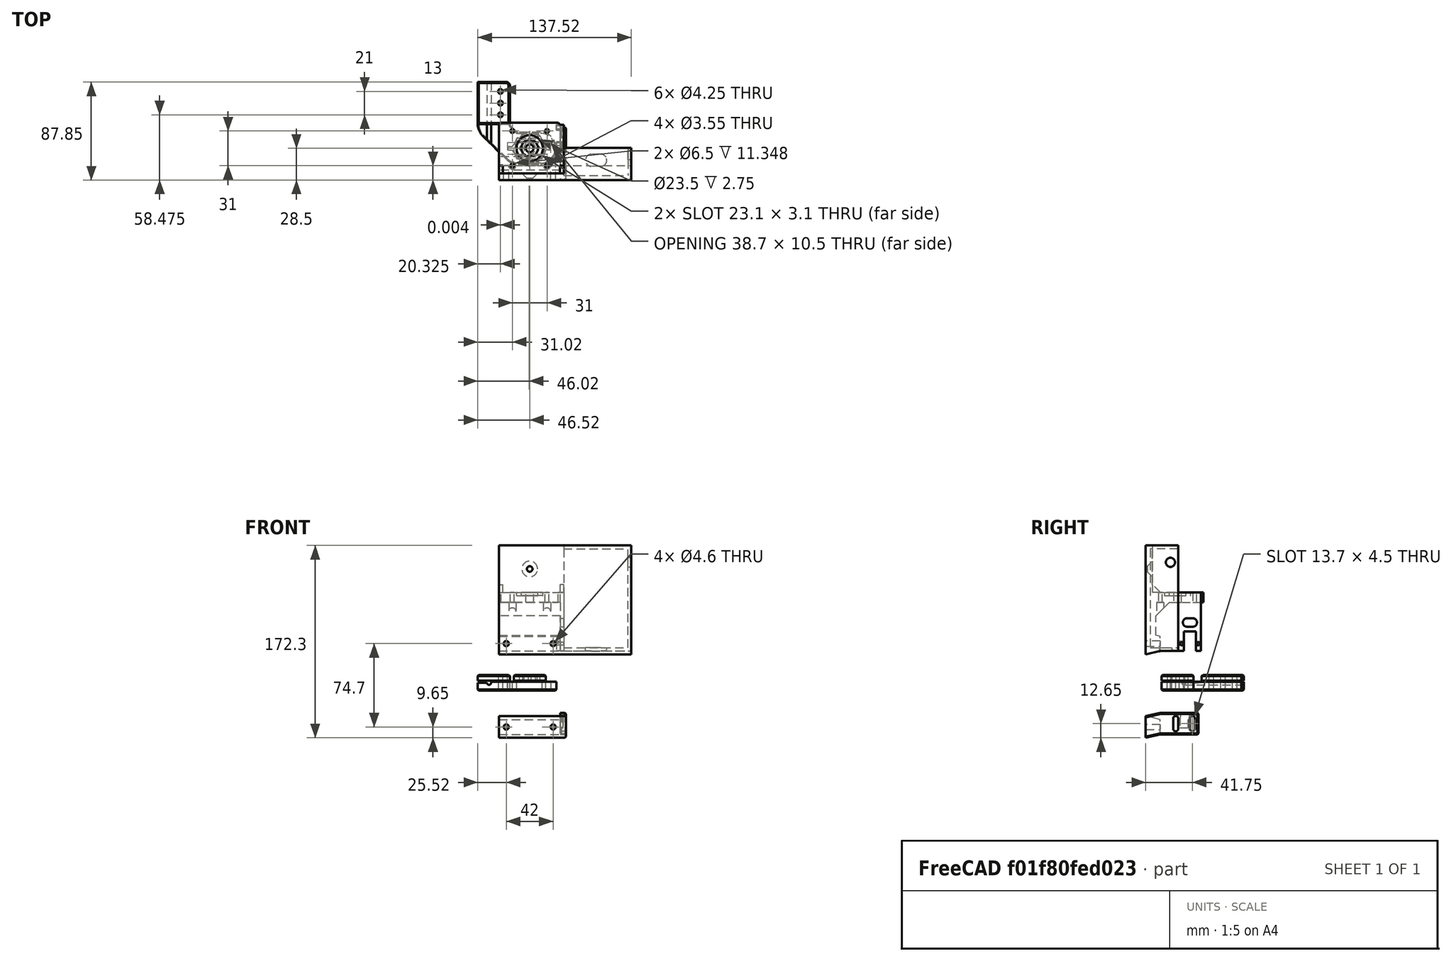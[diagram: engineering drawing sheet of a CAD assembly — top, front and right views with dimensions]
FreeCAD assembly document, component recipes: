
FREECAD ASSEMBLY — COMPONENT RECIPES ("Mount_Mk2")

This assembly document has 5 components, labeled P0..P4 below (a component is one placed body or linked part). 5 of them carry a construction recipe — the FreeCAD feature program that regenerates the part from scratch, quoted from this document or its linked companion documents; the rest are supplied as boundary geometry only. No exploded tour is included for this assembly.
COMPONENT P0 — recipe-attached ("Motor_Mount001", modeled in this document).
Construction recipe (the document's own serialized feature program — sketch geometry with constraints, then the solid features built on it; lengths are millimeters unless a unit is written):

FEATURE [Sketcher::SketchObject] Sketch002
  ArcFitTolerance = 1e-06
  AttachmentSupport = -> [XZ_Plane001]
  FullyConstrained = true
  MakeInternals = false
  MapMode = 5
  Placement = pos=(0,0,0) rot=(1,0,0;1.5708rad)
  sketch-geometry (32):
    g0: LineSegment StartX=0 StartY=0 StartZ=0 EndX=97.6 EndY=0 EndZ=0
    g1: LineSegment StartX=97.6 StartY=0 StartZ=0 EndX=94.6 EndY=13 EndZ=0
    g2: LineSegment StartX=94.6 StartY=13 StartZ=0 EndX=81.3 EndY=13 EndZ=0
    g3: LineSegment StartX=81.3 StartY=13 StartZ=0 EndX=80.3769 EndY=9 EndZ=0
    g4: LineSegment StartX=80.3769 StartY=9 StartZ=0 EndX=51.1 EndY=9 EndZ=0
    g5: LineSegment StartX=51.1 StartY=9 StartZ=0 EndX=51.1 EndY=51.55 EndZ=0
    g6: LineSegment StartX=51.1 StartY=51.55 StartZ=0 EndX=42.1 EndY=51.55 EndZ=0
    g7: LineSegment StartX=42.1 StartY=51.55 StartZ=0 EndX=42.1 EndY=6 EndZ=0
    g8: LineSegment StartX=42.1 StartY=6 StartZ=0 EndX=0 EndY=6 EndZ=0
    g9: LineSegment StartX=0 StartY=6 StartZ=0 EndX=0 EndY=0 EndZ=0
    g10: LineSegment [constr] StartX=94.6 StartY=13 StartZ=0 EndX=97.6 EndY=13 EndZ=0
    g11: LineSegment [constr] StartX=97.6 StartY=13 StartZ=0 EndX=97.6 EndY=0 EndZ=0
    g12: LineSegment [constr] StartX=80.3769 StartY=9 StartZ=0 EndX=78.3 EndY=0 EndZ=0
    g13: LineSegment [constr] StartX=78.3 StartY=0 StartZ=0 EndX=78.3 EndY=13 EndZ=0
    g14: LineSegment [constr] StartX=78.3 StartY=13 StartZ=0 EndX=81.3 EndY=13 EndZ=0
    g15: LineSegment [constr] StartX=81.3 StartY=13 StartZ=0 EndX=81.3 EndY=0 EndZ=0
    g16: LineSegment [constr] StartX=3 StartY=49.55 StartZ=0 EndX=42.3 EndY=49.55 EndZ=0
    g17: LineSegment [constr] StartX=42.3 StartY=7.45 StartZ=0 EndX=3 EndY=7.45 EndZ=0
    g18: LineSegment [constr] StartX=3 StartY=7.45 StartZ=0 EndX=3 EndY=49.55 EndZ=0
    g19: LineSegment [constr] StartX=42.3 StartY=45.5 StartZ=0 EndX=59.3 EndY=45.5 EndZ=0
    g20: LineSegment [constr] StartX=59.3 StartY=45.5 StartZ=0 EndX=59.3 EndY=42.5 EndZ=0
    g21: LineSegment [constr] StartX=59.3 StartY=42.5 StartZ=0 EndX=42.3 EndY=42.5 EndZ=0
    g22: LineSegment [constr] StartX=42.3 StartY=14.5 StartZ=0 EndX=59.3 EndY=14.5 EndZ=0
    g23: LineSegment [constr] StartX=59.3 StartY=14.5 StartZ=0 EndX=59.3 EndY=11.5 EndZ=0
    g24: LineSegment [constr] StartX=59.3 StartY=11.5 StartZ=0 EndX=42.3 EndY=11.5 EndZ=0
    g25: LineSegment [constr] StartX=42.3 StartY=49.55 StartZ=0 EndX=42.3 EndY=45.5 EndZ=0
    g26: LineSegment [constr] StartX=42.3 StartY=45.5 StartZ=0 EndX=42.3 EndY=42.5 EndZ=0
    g27: LineSegment [constr] StartX=42.3 StartY=42.5 StartZ=0 EndX=42.3 EndY=14.5 EndZ=0
    g28: LineSegment [constr] StartX=42.3 StartY=14.5 StartZ=0 EndX=42.3 EndY=11.5 EndZ=0
    g29: LineSegment [constr] StartX=42.3 StartY=11.5 StartZ=0 EndX=42.3 EndY=7.45 EndZ=0
    g30: LineSegment [constr] StartX=42.3 StartY=13 StartZ=0 EndX=59.3 EndY=13 EndZ=0
    g31: LineSegment [constr] StartX=42.3 StartY=44 StartZ=0 EndX=59.3 EndY=44 EndZ=0
  constraints (89):
    c: Coincident(g-1,g0)
    c: PointOnObject(g0,g-1)
    c: Coincident(g0,g1)
    c: Coincident(g1,g2)
    c: Horizontal(g2)
    c: Coincident(g2,g3)
    c: Coincident(g3,g4)
    c: Horizontal(g4)
    c: Coincident(g4,g5)
    c: Vertical(g5)
    c: Coincident(g5,g6)
    c: Horizontal(g6)
    c: Coincident(g6,g7)
    c: Vertical(g7)
    c: Coincident(g7,g8)
    c: PointOnObject(g8,g-2)
    c: Horizontal(g8)
    c: Coincident(g8,g9)
    c: Coincident(g9,g0)
    c: Coincident(g1,g10)
    c: Horizontal(g10)
    c: Coincident(g10,g11)
    c: Coincident(g11,g0)
    c: Vertical(g11)
    c: DistanceX(g2,g2) = 13.3
    c: Coincident(g3,g12)
    c: PointOnObject(g12,g0)
    c: Coincident(g12,g13)
    c: Vertical(g13)
    c: Coincident(g13,g14)
    c: Coincident(g14,g2)
    c: Parallel(g12,g3)
    c: Horizontal(g14)
    c: Equal(g14,g10)
    c: DistanceY(g11,g11) = 13
    c: Distance(g10,g10) = 3
    c: Coincident(g2,g15)
    c: PointOnObject(g15,g0)
    c: Vertical(g15)
    c: DistanceX(g6,g6) = 9
    c: DistanceY(g9,g9) = 6
    c: Horizontal(g16)
    c: Horizontal(g17)
    c: Coincident(g17,g18)
    c: Coincident(g18,g16)
    c: Vertical(g18)
    c: Horizontal(g19)
    c: Coincident(g19,g20)
    c: Vertical(g20)
    c: Coincident(g20,g21)
    c: Horizontal(g21)
    c: Horizontal(g22)
    c: Coincident(g22,g23)
    c: Vertical(g23)
    c: Coincident(g23,g24)
    c: Horizontal(g24)
    c: Equal(g19,g22)
    c: Equal(g20,g23)
    c: Coincident(g16,g25)
    c: Coincident(g25,g19)
    c: Vertical(g25)
    c: Coincident(g25,g26)
    c: Coincident(g26,g21)
    c: Vertical(g26)
    c: Coincident(g26,g27)
    c: Coincident(g27,g22)
    c: Vertical(g27)
    c: Coincident(g27,g28)
    c: Coincident(g28,g24)
    c: Vertical(g28)
    c: Coincident(g28,g29)
    c: Coincident(g29,g17)
    c: Vertical(g29)
    c: Equal(g25,g29)
    c: Symmetric(g28,g28,g30)
    c: Symmetric(g23,g23,g30)
    c: Symmetric(g26,g26,g31)
    c: Symmetric(g20,g20,g31)
    c: Distance(g31,g30) = 31
    c: DistanceY(g18,g18) = 42.1
    c: Distance(g7,g25) = 0.2
    c: Distance(g8,g30) = 7
    c: Distance(g6,g16) = 2
    c: DistanceX(g16,g16) = 39.3
    c: Distance(g18,g9) = 3
    c: Distance(g4,g30) = 4
    c: DistanceX(g19,g19) = 17
    c: DistanceY(g20,g20) = 3
    c: Distance(g15,g27) = 39
FEATURE [PartDesign::Pad] Pad001
  Direction = (0,-1,2e-16)
  Length = 55
  Length2 = 10
  Placement = pos=(0,0,0) rot=(1,0,0;1.5708rad)
  Profile = -> Sketch002
  ReferenceAxis = -> Sketch002 [N_Axis]
  Refine = true
  Suppressed = false
  Type = 0
FEATURE [Sketcher::SketchObject] Sketch003
  ArcFitTolerance = 1e-06
  AttachmentSupport = -> [Pad001]
  ExternalGeometry = -> [Pad001]
  FullyConstrained = true
  MakeInternals = false
  MapMode = 5
  Placement = pos=(42.1,0,0) rot=(0.707107,0,-0.707107;3.14159rad)
  sketch-geometry (13):
    g0: Circle CenterX=-44 CenterY=12 CenterZ=0 NormalX=0 NormalY=0 NormalZ=1 AngleXU=0 Radius=1.775
    g1: Circle CenterX=-44 CenterY=43 CenterZ=0 NormalX=0 NormalY=0 NormalZ=1 AngleXU=0 Radius=1.775
    g2: Circle CenterX=-13 CenterY=12 CenterZ=0 NormalX=0 NormalY=0 NormalZ=1 AngleXU=0 Radius=1.775
    g3: Circle CenterX=-13 CenterY=43 CenterZ=0 NormalX=0 NormalY=0 NormalZ=1 AngleXU=0 Radius=1.775
    g4: Circle CenterX=-28.5 CenterY=27.5 CenterZ=0 NormalX=0 NormalY=0 NormalZ=1 AngleXU=0 Radius=3.5
    g5: LineSegment [constr] StartX=-44 StartY=12 StartZ=0 EndX=-44 EndY=43 EndZ=0
    g6: LineSegment [constr] StartX=-44 StartY=43 StartZ=0 EndX=-13 EndY=43 EndZ=0
    g7: LineSegment [constr] StartX=-13 StartY=43 StartZ=0 EndX=-13 EndY=12 EndZ=0
    g8: LineSegment [constr] StartX=-13 StartY=12 StartZ=0 EndX=-44 EndY=12 EndZ=0
    g9: LineSegment [constr] StartX=-44 StartY=27.5 StartZ=0 EndX=-28.5 EndY=27.5 EndZ=0
    g10: LineSegment [constr] StartX=-28.5 StartY=27.5 StartZ=0 EndX=-28.5 EndY=12 EndZ=0
    g11: LineSegment [constr] StartX=-13 StartY=12 StartZ=0 EndX=-13 EndY=-3.6e-15 EndZ=0
    g12: LineSegment [constr] StartX=-13 StartY=43 StartZ=0 EndX=-13 EndY=55 EndZ=0
  constraints (33):
    c: Coincident(g5,g0)
    c: Coincident(g5,g1)
    c: Vertical(g5)
    c: Coincident(g5,g6)
    c: Coincident(g6,g3)
    c: Horizontal(g6)
    c: Coincident(g6,g7)
    c: Coincident(g7,g2)
    c: Vertical(g7)
    c: Coincident(g7,g8)
    c: Coincident(g8,g5)
    c: Horizontal(g8)
    c: Symmetric(g5,g5,g9)
    c: Coincident(g9,g4)
    c: Horizontal(g9)
    c: Coincident(g9,g10)
    c: Symmetric(g8,g8,g10)
    c: Vertical(g10)
    c: Equal(g6,g5)
    c: DistanceX(g6,g6) = 31
    c: Distance(g-5,g7) = 7
    c: Coincident(g11,g2)
    c: PointOnObject(g11,g-6)
    c: Vertical(g11)
    c: Coincident(g12,g3)
    c: Vertical(g12)
    c: Equal(g11,g12)
    c: Equal(g1,g0)
    c: Equal(g0,g3)
    c: Equal(g3,g2)
    c: Diameter(g1) = 3.55
    c: Diameter(g4) = 7
    c: PointOnObject(g12,g-3)
FEATURE [PartDesign::Pocket] Pocket001
  BaseFeature = -> Pad001
  Direction = (1,0,2e-16)
  Length = 0
  Length2 = 5
  Placement = pos=(0,0,0) rot=(1,0,0;1.5708rad)
  Profile = -> Sketch003
  ReferenceAxis = -> Sketch003 [N_Axis]
  Refine = true
  Suppressed = false
  Type = 3
  UpToFace = -> Pad001 [Face6]
FEATURE [Sketcher::SketchObject] Sketch004
  ArcFitTolerance = 1e-06
  AttachmentSupport = -> [Pocket001]
  ExternalGeometry = -> [Pocket001]
  FullyConstrained = true
  MakeInternals = false
  MapMode = 5
  Placement = pos=(42.1,0,0) rot=(0.707107,0,-0.707107;3.14159rad)
  sketch-geometry (2):
    g0: Circle CenterX=-28.5 CenterY=27.5 CenterZ=0 NormalX=0 NormalY=0 NormalZ=1 AngleXU=0 Radius=11.75
    g1: Circle CenterX=-28.5 CenterY=27.5 CenterZ=0 NormalX=0 NormalY=0 NormalZ=1 AngleXU=0 Radius=7.5
  constraints (4):
    c: Coincident(g0,g-3)
    c: Diameter(g0) = 23.5
    c: Coincident(g1,g0)
    c: Diameter(g1) = 15
FEATURE [PartDesign::Pocket] Pocket002
  BaseFeature = -> Pocket001
  Direction = (1,0,2e-16)
  Length = 2.75
  Length2 = 5
  Placement = pos=(0,0,0) rot=(1,0,0;1.5708rad)
  Profile = -> Sketch004
  ReferenceAxis = -> Sketch004 [N_Axis]
  Refine = true
  Suppressed = false
  Type = 0
FEATURE [Sketcher::SketchObject] Sketch005
  ArcFitTolerance = 1e-06
  AttachmentSupport = -> [Pocket002]
  ExternalGeometry = -> [Pocket002]
  FullyConstrained = true
  MakeInternals = false
  MapMode = 5
  Placement = pos=(0,5.7e-15,13) rot=(0,0,1;3.14159rad)
  sketch-geometry (5):
    g0: Circle CenterX=-87.95 CenterY=48.5 CenterZ=0 NormalX=0 NormalY=0 NormalZ=1 AngleXU=0 Radius=2.3
    g1: Circle CenterX=-87.95 CenterY=6.5 CenterZ=0 NormalX=0 NormalY=0 NormalZ=1 AngleXU=0 Radius=2.3
    g2: LineSegment [constr] StartX=-87.95 StartY=48.5 StartZ=0 EndX=-87.95 EndY=6.5 EndZ=0
    g3: LineSegment [constr] StartX=-87.95 StartY=48.5 StartZ=0 EndX=-87.95 EndY=55 EndZ=0
    g4: LineSegment [constr] StartX=-87.95 StartY=6.5 StartZ=0 EndX=-87.95 EndY=0 EndZ=0
  constraints (12):
    c: Coincident(g2,g0)
    c: Coincident(g2,g1)
    c: Vertical(g2)
    c: Coincident(g3,g0)
    c: Symmetric(g-3,g-3,g3)
    c: Coincident(g4,g1)
    c: Symmetric(g-6,g-6,g4)
    c: Vertical(g4)
    c: Equal(g3,g4)
    c: DistanceY(g2,g2) = 42
    c: Diameter(g0) = 4.6
    c: Equal(g0,g1)
FEATURE [PartDesign::Pocket] Pocket003
  BaseFeature = -> Pocket002
  Direction = (0,0,-1)
  Length = 5
  Length2 = 5
  Placement = pos=(0,0,0) rot=(1,0,0;1.5708rad)
  Profile = -> Sketch005
  ReferenceAxis = -> Sketch005 [N_Axis]
  Refine = true
  Suppressed = false
  Type = 1
FEATURE [PartDesign::Chamfer] Chamfer
  Angle = 45
  Base = -> Pocket003 [Edge15,Edge23]
  BaseFeature = -> Pocket003
  ChamferType = 0
  FlipDirection = false
  Placement = pos=(0,0,0) rot=(1,0,0;1.5708rad)
  Refine = true
  Size = 2
  Size2 = 1
  SupportTransform = false
  Suppressed = false
  UseAllEdges = false
FEATURE [Sketcher::SketchObject] Sketch006
  ArcFitTolerance = 1e-06
  AttachmentSupport = -> [Chamfer]
  ExternalGeometry = -> [Chamfer]
  FullyConstrained = true
  MakeInternals = false
  MapMode = 5
  Placement = pos=(0,2.6e-15,6) rot=(0,0,1;3.14159rad)
  sketch-geometry (3):
    g0: Circle CenterX=-21.05 CenterY=27.5 CenterZ=0 NormalX=0 NormalY=0 NormalZ=1 AngleXU=0 Radius=2.5
    g1: LineSegment [constr] StartX=-21.05 StartY=27.5 StartZ=0 EndX=0 EndY=27.5 EndZ=0
    g2: LineSegment [constr] StartX=-21.05 StartY=27.5 StartZ=0 EndX=-21.05 EndY=55 EndZ=0
  constraints (7):
    c: Coincident(g1,g0)
    c: Symmetric(g-4,g-4,g1)
    c: Horizontal(g1)
    c: Coincident(g2,g0)
    c: Symmetric(g-3,g-3,g2)
    c: Vertical(g2)
    c: Diameter(g0) = 5
FEATURE [PartDesign::Pocket] Pocket004
  BaseFeature = -> Chamfer
  Direction = (0,0,-1)
  Length = 5
  Length2 = 5
  Placement = pos=(0,0,0) rot=(1,0,0;1.5708rad)
  Profile = -> Sketch006
  ReferenceAxis = -> Sketch006 [N_Axis]
  Refine = true
  Suppressed = false
  Type = 1
FEATURE [PartDesign::Chamfer] Chamfer001
  Angle = 45
  Base = -> Pocket004 [Edge38]
  BaseFeature = -> Pocket004
  ChamferType = 0
  FlipDirection = false
  Placement = pos=(0,0,0) rot=(1,0,0;1.5708rad)
  Refine = true
  Size = 4.5
  Size2 = 1
  SupportTransform = false
  Suppressed = false
  UseAllEdges = false
FEATURE [Sketcher::SketchObject] Sketch011
  ArcFitTolerance = 1e-06
  AttachmentSupport = -> [Chamfer001]
  ExternalGeometry = -> [Chamfer001]
  FullyConstrained = true
  MakeInternals = false
  MapMode = 5
  Placement = pos=(0,-55,1.21e-14) rot=(1,0,0;1.5708rad)
  sketch-geometry (8):
    g0: LineSegment StartX=42.1 StartY=49.55 StartZ=0 EndX=51.1 EndY=49.55 EndZ=0
    g1: LineSegment StartX=94.6 StartY=13 StartZ=0 EndX=97.6 EndY=0 EndZ=0
    g2: LineSegment StartX=97.6 StartY=0 StartZ=0 EndX=0 EndY=0 EndZ=0
    g3: LineSegment StartX=0 StartY=0 StartZ=0 EndX=0 EndY=6 EndZ=0
    g4: LineSegment StartX=0 StartY=6 StartZ=0 EndX=42.1 EndY=6 EndZ=0
    g5: LineSegment StartX=42.1 StartY=6 StartZ=0 EndX=42.1 EndY=49.55 EndZ=0
    g6: LineSegment StartX=51.1 StartY=49.55 StartZ=0 EndX=94.6 EndY=49.55 EndZ=0
    g7: LineSegment StartX=94.6 StartY=49.55 StartZ=0 EndX=94.6 EndY=13 EndZ=0
  constraints (17):
    c: Coincident(g-12,g0)
    c: Coincident(g0,g-12)
    c: Coincident(g1,g-9)
    c: Coincident(g1,g2)
    c: Coincident(g2,g-1)
    c: Coincident(g2,g3)
    c: Coincident(g3,g-4)
    c: Coincident(g3,g4)
    c: Coincident(g4,g-6)
    c: Coincident(g4,g5)
    c: Coincident(g5,g0)
    c: Coincident(g0,g6)
    c: Horizontal(g6)
    c: Coincident(g6,g7)
    c: Coincident(g7,g1)
    c: Vertical(g7)
    c: Coincident(g-10,g1)
FEATURE [PartDesign::Pad] Pad005
  BaseFeature = -> Chamfer001
  Direction = (0,-1,2e-16)
  Length = 3
  Length2 = 10
  Placement = pos=(0,0,0) rot=(1,0,0;1.5708rad)
  Profile = -> Sketch011
  ReferenceAxis = -> Sketch011 [N_Axis]
  Refine = true
  Suppressed = false
  Type = 0
FEATURE [Sketcher::SketchObject] Sketch012
  ArcFitTolerance = 1e-06
  AttachmentSupport = -> [Pad005]
  ExternalGeometry = -> [Pad005]
  FullyConstrained = true
  MakeInternals = false
  MapMode = 5
  Placement = pos=(0,-58,1.74e-14) rot=(1,0,0;1.5708rad)
  sketch-geometry (11):
    g0: LineSegment StartX=97.6 StartY=-5.3e-15 StartZ=0 EndX=0 EndY=0 EndZ=0
    g1: LineSegment StartX=0 StartY=0 StartZ=0 EndX=5e-16 EndY=4 EndZ=0
    g2: LineSegment [constr] StartX=5e-16 StartY=4 StartZ=0 EndX=96.6769 EndY=4 EndZ=0
    g3: LineSegment StartX=5e-16 StartY=4 StartZ=0 EndX=0 EndY=29 EndZ=0
    g4: LineSegment StartX=0 StartY=29 StartZ=0 EndX=3 EndY=29 EndZ=0
    g5: LineSegment StartX=3 StartY=29 StartZ=0 EndX=3 EndY=4 EndZ=0
    g6: LineSegment StartX=3 StartY=4 StartZ=0 EndX=91.6 EndY=4 EndZ=0
    g7: LineSegment StartX=91.6 StartY=4 StartZ=0 EndX=91.6 EndY=29 EndZ=0
    g8: LineSegment StartX=91.6 StartY=29 StartZ=0 EndX=94.6 EndY=29 EndZ=0
    g9: LineSegment StartX=97.6 StartY=-5.3e-15 StartZ=0 EndX=94.6 EndY=13 EndZ=0
    g10: LineSegment StartX=94.6 StartY=13 StartZ=0 EndX=94.6 EndY=29 EndZ=0
  constraints (31):
    c: Coincident(g0,g-1)
    c: Coincident(g0,g1)
    c: PointOnObject(g1,g-4)
    c: Coincident(g1,g2)
    c: Horizontal(g2)
    c: Distance(g1,g1) = 4
    c: Coincident(g1,g3)
    c: PointOnObject(g3,g-2)
    c: Coincident(g3,g4)
    c: Horizontal(g4)
    c: Coincident(g4,g5)
    c: PointOnObject(g5,g2)
    c: Vertical(g5)
    c: Coincident(g5,g6)
    c: PointOnObject(g6,g2)
    c: Coincident(g6,g7)
    c: Vertical(g7)
    c: Distance(g4,g4) = 3
    c: Equal(g3,g7)
    c: Distance(g3,g3) = 25
    c: Coincident(g7,g8)
    c: Horizontal(g8)
    c: Equal(g4,g8)
    c: DistanceX(g6,g6) = 88.6
    c: Coincident(g0,g9)
    c: Coincident(g9,g-7)
    c: Coincident(g9,g10)
    c: Coincident(g10,g8)
    c: PointOnObject(g8,g-7)
    c: Coincident(g0,g-6)
    c: PointOnObject(g2,g9)
FEATURE [PartDesign::Pad] Pad006
  BaseFeature = -> Pad005
  Direction = (0,-1,2e-16)
  Length = 57.5
  Length2 = 10
  Placement = pos=(0,0,0) rot=(1,0,0;1.5708rad)
  Profile = -> Sketch012
  ReferenceAxis = -> Sketch012 [N_Axis]
  Refine = true
  Suppressed = false
  Type = 0
FEATURE [Sketcher::SketchObject] Sketch013
  ArcFitTolerance = 1e-06
  AttachmentSupport = -> [Pad006]
  ExternalGeometry = -> [Pad006]
  FullyConstrained = true
  MakeInternals = false
  MapMode = 5
  Placement = pos=(0,-115.5,2.89e-14) rot=(1,0,0;1.5708rad)
  sketch-geometry (9):
    g0: LineSegment StartX=94.6 StartY=13 StartZ=0 EndX=94.6 EndY=29 EndZ=0
    g1: LineSegment StartX=94.6 StartY=29 StartZ=0 EndX=94.6 EndY=29 EndZ=0
    g2: LineSegment StartX=94.6 StartY=29 StartZ=0 EndX=0 EndY=29 EndZ=0
    g3: LineSegment StartX=0 StartY=29 StartZ=0 EndX=0 EndY=-3.6e-15 EndZ=0
    g4: Circle CenterX=15.1 CenterY=22.1 CenterZ=0 NormalX=0 NormalY=0 NormalZ=1 AngleXU=0 Radius=4.1
    g5: LineSegment [constr] StartX=11 StartY=22.1 StartZ=0 EndX=3 EndY=22.1 EndZ=0
    g6: LineSegment [constr] StartX=15.1 StartY=18 StartZ=0 EndX=15.1 EndY=4 EndZ=0
    g7: LineSegment StartX=0 StartY=-3.6e-15 StartZ=0 EndX=97.6 EndY=-3.6e-15 EndZ=0
    g8: LineSegment StartX=94.6 StartY=13 StartZ=0 EndX=97.6 EndY=-3.6e-15 EndZ=0
  constraints (23):
    c: Coincident(g0,g-6)
    c: Coincident(g0,g1)
    c: Coincident(g1,g-7)
    c: Coincident(g1,g2)
    c: Coincident(g2,g-8)
    c: Coincident(g2,g3)
    c: Diameter(g4) = 8.2
    c: PointOnObject(g5,g4)
    c: PointOnObject(g5,g-10)
    c: Horizontal(g5)
    c: PointOnObject(g6,g4)
    c: PointOnObject(g6,g-9)
    c: Vertical(g6)
    c: Perpendicular(g4,g6)
    c: Perpendicular(g4,g5)
    c: DistanceX(g5,g5) = 8
    c: DistanceY(g6,g6) = 14
    c: Coincident(g7,g3)
    c: Coincident(g7,g-5)
    c: Coincident(g8,g0)
    c: Coincident(g8,g7)
    c: Coincident(g-6,g0)
    c: Coincident(g3,g-1)
FEATURE [PartDesign::Pad] Pad007
  BaseFeature = -> Pad006
  Direction = (0,-1,2e-16)
  Length = 3
  Length2 = 10
  Placement = pos=(0,0,0) rot=(1,0,0;1.5708rad)
  Profile = -> Sketch013
  ReferenceAxis = -> Sketch013 [N_Axis]
  Refine = true
  Suppressed = false
  Type = 0
FEATURE [Sketcher::SketchObject] Sketch014
  ArcFitTolerance = 1e-06
  AttachmentSupport = -> [Pad007]
  ExternalGeometry = -> [Pad007]
  FullyConstrained = true
  MakeInternals = false
  MapMode = 5
  Placement = pos=(0,-55,1.65e-14) rot=(-1,0,0;1.5708rad)
  sketch-geometry (3):
    g0: LineSegment StartX=63.1208 StartY=-9 StartZ=0 EndX=51.1 EndY=-9 EndZ=0
    g1: LineSegment StartX=51.1 StartY=-9 StartZ=0 EndX=51.1 EndY=-21.0208 EndZ=0
    g2: LineSegment StartX=51.1 StartY=-21.0208 StartZ=0 EndX=63.1208 EndY=-9 EndZ=0
  constraints (8):
    c: PointOnObject(g0,g-3)
    c: Coincident(g0,g-4)
    c: Coincident(g0,g1)
    c: PointOnObject(g1,g-4)
    c: Coincident(g1,g2)
    c: Coincident(g2,g0)
    c: Equal(g1,g0)
    c: Distance(g0,g2) = 8.5
FEATURE [PartDesign::Pad] Pad008
  BaseFeature = -> Pad007
  Direction = (0,1,2e-16)
  Length = 10
  Length2 = 10
  Placement = pos=(0,0,0) rot=(1,0,0;1.5708rad)
  Profile = -> Sketch014
  ReferenceAxis = -> Sketch014 [N_Axis]
  Refine = true
  Suppressed = false
  Type = 3
  UpToFace = -> Pad007 [Face6]
FEATURE [PartDesign::Hole] Hole
  BaseFeature = -> Pad008
  CustomThreadClearance = 0
  Depth = 25
  DepthType = 0
  Diameter = 6.5
  DrillForDepth = false
  DrillPoint = 1
  DrillPointAngle = 118
  HoleCutCountersinkAngle = 90
  HoleCutCustomValues = false
  HoleCutDepth = 0
  HoleCutDiameter = 6.1
  HoleCutType = 0
  ModelThread = false
  Placement = pos=(0,0,0) rot=(1,0,0;1.5708rad)
  Profile = -> Pad008 [Face30,Face31]
  Refine = true
  Suppressed = false
  Tapered = false
  TaperedAngle = 90
  ThreadClass = 0
  ThreadDepth = 25
  ThreadDepthType = 0
  ThreadDirection = 0
  ThreadFit = 0
  ThreadSize = 0
  ThreadType = 0
  Threaded = false
  UseCustomThreadClearance = false
FEATURE [Sketcher::SketchObject] Sketch015
  ArcFitTolerance = 1e-06
  AttachmentSupport = -> [Hole]
  ExternalGeometry = -> [Hole]
  FullyConstrained = true
  MakeInternals = false
  MapMode = 5
  Placement = pos=(0,-58,1.45e-14) rot=(-1,0,0;1.5708rad)
  sketch-geometry (3):
    g0: LineSegment StartX=94.6 StartY=-13 StartZ=0 EndX=94.6 EndY=-29 EndZ=0
    g1: LineSegment StartX=94.6 StartY=-29 StartZ=0 EndX=94.6 EndY=-29 EndZ=0
    g2: LineSegment StartX=94.6 StartY=-29 StartZ=0 EndX=94.6 EndY=-13 EndZ=0
  constraints (7):
    c: Coincident(g-4,g0)
    c: Coincident(g0,g-6)
    c: Coincident(g0,g1)
    c: PointOnObject(g1,g-5)
    c: Coincident(g1,g2)
    c: Coincident(g2,g0)
    c: Horizontal(g1)
FEATURE [Sketcher::SketchObject] Sketch016
  ArcFitTolerance = 1e-06
  FullyConstrained = true
  MakeInternals = false
  MapMode = 5
  Placement = pos=(91.6,0,0) rot=(0.707107,0,-0.707107;3.14159rad)
  sketch-geometry (9):
    g0: ArcOfCircle CenterX=-17.75 CenterY=91 CenterZ=0 NormalX=0 NormalY=0 NormalZ=1 AngleXU=0 Radius=5.5 StartAngle=0 EndAngle=3.14159
    g1: ArcOfCircle CenterX=-17.75 CenterY=83 CenterZ=0 NormalX=0 NormalY=0 NormalZ=1 AngleXU=0 Radius=5.5 StartAngle=3.14159 EndAngle=6.28319
    g2: LineSegment StartX=-12.25 StartY=91 StartZ=0 EndX=-12.25 EndY=83 EndZ=0
    g3: LineSegment StartX=-23.25 StartY=91 StartZ=0 EndX=-23.25 EndY=83 EndZ=0
    g4: LineSegment [constr] StartX=-17.75 StartY=77.5 StartZ=0 EndX=-17.75 EndY=83 EndZ=0
    g5: LineSegment [constr] StartX=-17.75 StartY=83 StartZ=0 EndX=-17.75 EndY=91 EndZ=0
    g6: LineSegment [constr] StartX=-17.75 StartY=91 StartZ=0 EndX=-17.75 EndY=96.5 EndZ=0
    g7: LineSegment [constr] StartX=-17.75 StartY=77.5 StartZ=0 EndX=-17.75 EndY=58 EndZ=0
    g8: LineSegment [constr] StartX=-17.75 StartY=96.5 StartZ=0 EndX=-17.75 EndY=115.5 EndZ=0
  constraints (25):
    c: Tangent(g0,g2) = 1.5708
    c: Tangent(g0,g3) = -1.5708
    c: Tangent(g1,g2) = 1.5708
    c: Tangent(g1,g3) = -1.5708
    c: Equal(g0,g1)
    c: Vertical(g2)
    c: PointOnObject(g4,g1)
    c: Coincident(g4,g1)
    c: Coincident(g5,g1)
    c: Coincident(g5,g0)
    c: Coincident(g6,g0)
    c: PointOnObject(g6,g0)
    c: Vertical(g6)
    c: Vertical(g4)
    c: DistanceY(g4,g6) = 19
    c: DistanceX(g0,g0) = 11
    c: PointOnObject(g7,g-6)
    c: Vertical(g7)
    c: Coincident(g8,g6)
    c: PointOnObject(g8,g-3)
    c: Vertical(g8)
    c: Coincident(g7,g4)
    c: DistanceY(g8,g8) = 19
    c: DistanceY(g7,g7) = 19.5
    c: Distance(g1,g-4) = 13.75
FEATURE [PartDesign::Pocket] Pocket006
  BaseFeature = -> Hole
  Direction = (1,0,2e-16)
  Length = 5
  Length2 = 5
  Placement = pos=(0,0,0) rot=(1,0,0;1.5708rad)
  Profile = -> Sketch016
  ReferenceAxis = -> Sketch016 [N_Axis]
  Refine = true
  Suppressed = false
  Type = 1
FEATURE [Sketcher::SketchObject] Sketch017
  ArcFitTolerance = 1e-06
  AttachmentSupport = -> [Pocket006]
  ExternalGeometry = -> [Pocket006]
  FullyConstrained = true
  MakeInternals = false
  MapMode = 5
  Placement = pos=(0,-3e-16,0) rot=(-1,0,0;1.5708rad)
  sketch-geometry (3):
    g0: LineSegment StartX=42.1 StartY=-6 StartZ=0 EndX=35.0289 EndY=-6 EndZ=0
    g1: LineSegment StartX=35.0289 StartY=-6 StartZ=0 EndX=42.1 EndY=-13.0711 EndZ=0
    g2: LineSegment StartX=42.1 StartY=-13.0711 StartZ=0 EndX=42.1 EndY=-6 EndZ=0
  constraints (8):
    c: Coincident(g-4,g0)
    c: Horizontal(g0)
    c: Coincident(g0,g1)
    c: PointOnObject(g1,g-4)
    c: Coincident(g1,g2)
    c: Coincident(g2,g0)
    c: Equal(g0,g2)
    c: Distance(g0,g1) = 5
FEATURE [PartDesign::Pad] Pad010
  BaseFeature = -> Pocket006
  Direction = (0,1,2e-16)
  Length = 3.5
  Length2 = 10
  Placement = pos=(0,0,0) rot=(1,0,0;1.5708rad)
  Profile = -> Sketch017
  ReferenceAxis = -> Sketch017 [N_Axis]
  Refine = true
  Reversed = true
  Suppressed = false
  Type = 0
FEATURE [Sketcher::SketchObject] Sketch018
  ArcFitTolerance = 1e-06
  AttachmentSupport = -> [Pad010]
  ExternalGeometry = -> [Pad010]
  FullyConstrained = true
  MakeInternals = false
  MapMode = 5
  Placement = pos=(0,-58,1.74e-14) rot=(1,0,0;1.5708rad)
  sketch-geometry (3):
    g0: LineSegment StartX=35.0289 StartY=6 StartZ=0 EndX=42.1 EndY=6 EndZ=0
    g1: LineSegment StartX=42.1 StartY=6 StartZ=0 EndX=42.1 EndY=13.0711 EndZ=0
    g2: LineSegment StartX=42.1 StartY=13.0711 StartZ=0 EndX=35.0289 EndY=6 EndZ=0
  constraints (8):
    c: PointOnObject(g0,g-4)
    c: Coincident(g0,g-4)
    c: Coincident(g0,g1)
    c: PointOnObject(g1,g-3)
    c: Coincident(g1,g2)
    c: Coincident(g2,g0)
    c: Equal(g0,g1)
    c: Distance(g0,g2) = 5
FEATURE [PartDesign::Pad] Pad011
  BaseFeature = -> Pad010
  Direction = (0,-1,2e-16)
  Length = 3.5
  Length2 = 10
  Placement = pos=(0,0,0) rot=(1,0,0;1.5708rad)
  Profile = -> Sketch018
  ReferenceAxis = -> Sketch018 [N_Axis]
  Refine = true
  Reversed = true
  Suppressed = false
  Type = 0
FEATURE [Sketcher::SketchObject] Sketch019
  ArcFitTolerance = 1e-06
  AttachmentSupport = -> [Pad011]
  ExternalGeometry = -> [Pad011]
  FullyConstrained = true
  MakeInternals = false
  MapMode = 5
  Placement = pos=(0,-55,1.65e-14) rot=(-1,0,0;1.5708rad)
  sketch-geometry (24):
    g0: Circle [constr] CenterX=88.1 CenterY=-47.13 CenterZ=0 NormalX=0 NormalY=0 NormalZ=1 AngleXU=0 Radius=1.5
    g1: Circle [constr] CenterX=88.1 CenterY=-32.04 CenterZ=0 NormalX=0 NormalY=0 NormalZ=1 AngleXU=0 Radius=1.5
    g2: LineSegment [constr] StartX=88.1 StartY=-32.04 StartZ=0 EndX=88.1 EndY=-30.54 EndZ=0
    g3: LineSegment [constr] StartX=88.1 StartY=-30.54 StartZ=0 EndX=88.1 EndY=-13 EndZ=0
    g4: LineSegment [constr] StartX=88.1 StartY=-47.13 StartZ=0 EndX=88.1 EndY=-45.63 EndZ=0
    g5: LineSegment [constr] StartX=88.1 StartY=-45.63 StartZ=0 EndX=88.1 EndY=-33.54 EndZ=0
    g6: LineSegment [constr] StartX=88.1 StartY=-33.54 StartZ=0 EndX=88.1 EndY=-32.04 EndZ=0
    g7: LineSegment StartX=94.6 StartY=-44.88 StartZ=0 EndX=88.1 EndY=-44.88 EndZ=0
    g8: LineSegment StartX=88.1 StartY=-44.88 StartZ=0 EndX=85.85 EndY=-44.88 EndZ=0
    g9: LineSegment StartX=85.85 StartY=-44.88 StartZ=0 EndX=85.85 EndY=-49.55 EndZ=0
    g10: LineSegment [constr] StartX=88.1 StartY=-45.63 StartZ=0 EndX=88.1 EndY=-44.88 EndZ=0
    g11: LineSegment [constr] StartX=86.6 StartY=-47.13 StartZ=0 EndX=85.85 EndY=-47.13 EndZ=0
    g12: LineSegment StartX=85.85 StartY=-49.55 StartZ=0 EndX=94.6 EndY=-49.55 EndZ=0
    g13: LineSegment StartX=94.6 StartY=-44.88 StartZ=0 EndX=94.6 EndY=-49.55 EndZ=0
    g14: Circle CenterX=88.1 CenterY=-47.13 CenterZ=0 NormalX=0 NormalY=0 NormalZ=1 AngleXU=0 Radius=1.4
    g15: Circle CenterX=88.1 CenterY=-32.04 CenterZ=0 NormalX=0 NormalY=0 NormalZ=1 AngleXU=0 Radius=1.4
    g16: LineSegment StartX=94.6 StartY=-34.29 StartZ=0 EndX=85.85 EndY=-34.29 EndZ=0
    g17: LineSegment StartX=85.85 StartY=-34.29 StartZ=0 EndX=85.85 EndY=-28.54 EndZ=0
    g18: LineSegment StartX=85.85 StartY=-28.54 StartZ=0 EndX=94.6 EndY=-28.54 EndZ=0
    g19: LineSegment StartX=94.6 StartY=-34.29 StartZ=0 EndX=94.6 EndY=-28.54 EndZ=0
    g20: LineSegment [constr] StartX=88.1 StartY=-33.54 StartZ=0 EndX=88.1 EndY=-34.29 EndZ=0
    g21: LineSegment [constr] StartX=86.6 StartY=-32.04 StartZ=0 EndX=85.85 EndY=-32.04 EndZ=0
    g22: LineSegment [constr] StartX=88.1 StartY=-30.54 StartZ=0 EndX=88.1 EndY=-28.54 EndZ=0
    g23: LineSegment [constr] StartX=89.6 StartY=-32.04 StartZ=0 EndX=94.6 EndY=-32.04 EndZ=0
  constraints (72):
    c: Equal(g1,g0)
    c: DistanceX(g-3,g-3) = 13.3
    c: Coincident(g2,g1)
    c: PointOnObject(g2,g1)
    c: Vertical(g2)
    c: PointOnObject(g3,g-3)
    c: Vertical(g3)
    c: Coincident(g3,g2)
    c: Distance(g0,g-4) = 6.5
    c: DistanceY(g3,g3) = 17.54
    c: Coincident(g4,g0)
    c: PointOnObject(g4,g0)
    c: Vertical(g4)
    c: Coincident(g4,g5)
    c: PointOnObject(g5,g1)
    c: Vertical(g5)
    c: Coincident(g5,g6)
    c: Coincident(g6,g1)
    c: Vertical(g6)
    c: DistanceY(g5,g5) = 12.09
    c: Diameter(g0) = 3
    c: PointOnObject(g7,g5)
    c: Horizontal(g7)
    c: Coincident(g7,g8)
    c: Horizontal(g8)
    c: Coincident(g8,g9)
    c: Vertical(g9)
    c: Coincident(g10,g4)
    c: Coincident(g10,g7)
    c: PointOnObject(g11,g9)
    c: Horizontal(g11)
    c: PointOnObject(g11,g0)
    c: Perpendicular(g0,g11)
    c: Equal(g10,g11)
    c: PointOnObject(g9,g-5)
    c: PointOnObject(g7,g-4)
    c: Coincident(g12,g9)
    c: Coincident(g12,g-5)
    c: Coincident(g13,g7)
    c: Coincident(g13,g12)
    c: Coincident(g14,g0)
    c: Diameter(g14) = 2.8
    c: DistanceY(g10,g10) = 0.75
    c: Coincident(g15,g1)
    c: Equal(g15,g14)
    c: PointOnObject(g16,g-4)
    c: Horizontal(g16)
    c: Coincident(g16,g17)
    c: Vertical(g17)
    c: Coincident(g17,g18)
    c: PointOnObject(g18,g-4)
    c: Horizontal(g18)
    c: Coincident(g19,g16)
    c: Coincident(g19,g18)
    c: Coincident(g20,g6)
    c: PointOnObject(g20,g16)
    c: Vertical(g20)
    c: PointOnObject(g21,g1)
    c: PointOnObject(g21,g17)
    c: Horizontal(g21)
    c: Perpendicular(g1,g21)
    c: Equal(g20,g21)
    c: Equal(g20,g10)
    c: Coincident(g22,g2)
    c: PointOnObject(g22,g18)
    c: Vertical(g22)
    c: DistanceY(g22,g22) = 2
    c: PointOnObject(g23,g1)
    c: PointOnObject(g23,g19)
    c: Horizontal(g23)
    c: Perpendicular(g1,g23)
    c: DistanceX(g23,g23) = 5
FEATURE [PartDesign::Pad] Pad012
  BaseFeature = -> Pad011
  Direction = (0,1,2e-16)
  Length = 3.5
  Length2 = 10
  Placement = pos=(0,0,0) rot=(1,0,0;1.5708rad)
  Profile = -> Sketch019
  ReferenceAxis = -> Sketch019 [N_Axis]
  Refine = true
  Suppressed = false
  Type = 0
FEATURE [Sketcher::SketchObject] Sketch020
  ArcFitTolerance = 1e-06
  AttachmentSupport = -> [Pad012]
  ExternalGeometry = -> [Pad012]
  FullyConstrained = true
  MakeInternals = false
  MapMode = 5
  Placement = pos=(0,-55,1.65e-14) rot=(-1,0,0;1.5708rad)
  sketch-geometry (24):
    g0: ArcOfCircle CenterX=69.0132 CenterY=-37.0994 CenterZ=0 NormalX=0 NormalY=0 NormalZ=1 AngleXU=0 Radius=3.83685 StartAngle=1e-15 EndAngle=3.14159
    g1: ArcOfCircle CenterX=69.0132 CenterY=-42.0706 CenterZ=0 NormalX=0 NormalY=0 NormalZ=1 AngleXU=0 Radius=3.83685 StartAngle=3.14159 EndAngle=6.28319
    g2: LineSegment StartX=72.85 StartY=-37.0994 StartZ=0 EndX=72.85 EndY=-42.0706 EndZ=0
    g3: LineSegment StartX=65.1763 StartY=-37.0994 StartZ=0 EndX=65.1763 EndY=-42.0706 EndZ=0
    g4: LineSegment [constr] StartX=69.0132 StartY=-37.0994 StartZ=0 EndX=69.0132 EndY=-33.2625 EndZ=0
    g5: LineSegment [constr] StartX=69.0132 StartY=-37.0994 StartZ=0 EndX=69.0132 EndY=-42.0706 EndZ=0
    g6: LineSegment [constr] StartX=69.0132 StartY=-42.0706 StartZ=0 EndX=69.0132 EndY=-45.9075 EndZ=0
    g7: LineSegment [constr] StartX=71.8382 StartY=-43.2 StartZ=0 EndX=71.8382 EndY=-35.97 EndZ=0
    g8: LineSegment [constr] StartX=71.8382 StartY=-35.97 StartZ=0 EndX=66.1882 EndY=-35.97 EndZ=0
    g9: LineSegment [constr] StartX=66.1882 StartY=-35.97 StartZ=0 EndX=66.1882 EndY=-43.2 EndZ=0
    g10: LineSegment [constr] StartX=66.1882 StartY=-43.2 StartZ=0 EndX=71.8382 EndY=-43.2 EndZ=0
    g11: LineSegment [constr] StartX=72.4382 StartY=-43.8 StartZ=0 EndX=72.4382 EndY=-35.37 EndZ=0
    g12: LineSegment [constr] StartX=72.4382 StartY=-35.37 StartZ=0 EndX=65.5882 EndY=-35.37 EndZ=0
    g13: LineSegment [constr] StartX=65.5882 StartY=-35.37 StartZ=0 EndX=65.5882 EndY=-43.8 EndZ=0
    g14: LineSegment [constr] StartX=65.5882 StartY=-43.8 StartZ=0 EndX=72.4382 EndY=-43.8 EndZ=0
    g15: LineSegment [constr] StartX=71.8382 StartY=-43.2 StartZ=0 EndX=72.4382 EndY=-43.8 EndZ=0
    g16: LineSegment [constr] StartX=71.8382 StartY=-35.97 StartZ=0 EndX=72.4382 EndY=-35.37 EndZ=0
    g17: LineSegment [constr] StartX=66.1882 StartY=-35.97 StartZ=0 EndX=65.5882 EndY=-35.37 EndZ=0
    g18: LineSegment [constr] StartX=66.1882 StartY=-43.2 StartZ=0 EndX=65.5882 EndY=-43.8 EndZ=0
    g19: LineSegment [constr] StartX=66.1882 StartY=-43.2 StartZ=0 EndX=65.5882 EndY=-43.2 EndZ=0
    g20: Circle CenterX=88.1 CenterY=-47.13 CenterZ=0 NormalX=0 NormalY=0 NormalZ=1 AngleXU=0 Radius=1.4
    g21: Circle CenterX=88.1 CenterY=-32.04 CenterZ=0 NormalX=0 NormalY=0 NormalZ=1 AngleXU=0 Radius=1.4
    g22: LineSegment [constr] StartX=85.85 StartY=-44.88 StartZ=0 EndX=85.85 EndY=-34.29 EndZ=0
    g23: LineSegment [constr] StartX=85.85 StartY=-39.585 StartZ=0 EndX=72.85 EndY=-39.585 EndZ=0
  constraints (62):
    c: Tangent(g0,g2) = 1.5708
    c: Tangent(g0,g3) = -1.5708
    c: Tangent(g1,g2) = 1.5708
    c: Tangent(g1,g3) = -1.5708
    c: Equal(g0,g1)
    c: Vertical(g2)
    c: Coincident(g4,g0)
    c: PointOnObject(g4,g0)
    c: Vertical(g4)
    c: Coincident(g5,g0)
    c: Coincident(g5,g1)
    c: Coincident(g6,g1)
    c: PointOnObject(g6,g1)
    c: Vertical(g6)
    c: Coincident(g7,g8)
    c: Coincident(g8,g9)
    c: Coincident(g9,g10)
    c: Coincident(g10,g7)
    c: Vertical(g7)
    c: Vertical(g9)
    c: Horizontal(g8)
    c: Horizontal(g10)
    c: Coincident(g11,g12)
    c: Coincident(g12,g13)
    c: Coincident(g13,g14)
    c: Coincident(g14,g11)
    c: Vertical(g11)
    c: Vertical(g13)
    c: Horizontal(g12)
    c: Horizontal(g14)
    c: Coincident(g15,g7)
    c: Coincident(g15,g11)
    c: Coincident(g16,g8)
    c: Coincident(g16,g12)
    c: Coincident(g17,g9)
    c: Coincident(g17,g13)
    c: Coincident(g18,g10)
    c: Coincident(g18,g14)
    c: Perpendicular(g15,g16)
    c: Perpendicular(g16,g17)
    c: Perpendicular(g17,g18)
    c: Coincident(g19,g9)
    c: PointOnObject(g19,g13)
    c: Horizontal(g19)
    c: DistanceX(g19,g19) = 0.6
    c: PointOnObject(g11,g1)
    c: PointOnObject(g13,g1)
    c: PointOnObject(g12,g0)
    c: DistanceX(g10,g10) = 5.65
    c: DistanceY(g7,g7) = 7.23
    c: DistanceY(g3,g3) = 4.97124
    c: Radius(g0) = 3.83685
    c: Coincident(g20,g-9)
    c: Equal(g20,g-9)
    c: Coincident(g21,g-10)
    c: Equal(g21,g-10)
    c: Coincident(g22,g-8)
    c: Coincident(g22,g-6)
    c: Symmetric(g22,g22,g23)
    c: Symmetric(g2,g2,g23)
    c: Horizontal(g23)
    c: DistanceX(g23,g23) = 13
FEATURE [PartDesign::Pocket] Pocket007
  BaseFeature = -> Pad012
  Direction = (0,-1,-2e-16)
  Length = 5
  Length2 = 5
  Placement = pos=(0,0,0) rot=(1,0,0;1.5708rad)
  Profile = -> Sketch020
  ReferenceAxis = -> Sketch020 [N_Axis]
  Refine = true
  Suppressed = false
  Type = 0
FEATURE [Sketcher::SketchObject] Sketch021
  ArcFitTolerance = 1e-06
  AttachmentSupport = -> [Pad012]
  ExternalGeometry = -> [Pad012]
  FullyConstrained = true
  MakeInternals = false
  MapMode = 5
  Placement = pos=(0,-55,1.65e-14) rot=(-1,0,0;1.5708rad)
  sketch-geometry (6):
    g0: LineSegment StartX=94.6 StartY=-34.29 StartZ=0 EndX=94.6 EndY=-44.88 EndZ=0
    g1: LineSegment StartX=94.6 StartY=-44.88 StartZ=0 EndX=85.85 EndY=-44.88 EndZ=0
    g2: LineSegment StartX=85.85 StartY=-44.88 StartZ=0 EndX=76.85 EndY=-44.88 EndZ=0
    g3: LineSegment StartX=76.85 StartY=-44.88 StartZ=0 EndX=76.85 EndY=-34.29 EndZ=0
    g4: LineSegment StartX=76.85 StartY=-34.29 StartZ=0 EndX=85.85 EndY=-34.29 EndZ=0
    g5: LineSegment StartX=85.85 StartY=-34.29 StartZ=0 EndX=94.6 EndY=-34.29 EndZ=0
  constraints (14):
    c: Coincident(g-5,g0)
    c: Coincident(g0,g-5)
    c: Coincident(g0,g1)
    c: Coincident(g1,g-4)
    c: Coincident(g1,g2)
    c: Horizontal(g2)
    c: Coincident(g2,g3)
    c: Vertical(g3)
    c: Coincident(g3,g4)
    c: Coincident(g4,g-3)
    c: Horizontal(g4)
    c: Coincident(g4,g5)
    c: Coincident(g5,g0)
    c: DistanceX(g4,g4) = 9
FEATURE [PartDesign::Pocket] Pocket008
  BaseFeature = -> Pocket007
  Direction = (0,-1,-2e-16)
  Length = 5
  Length2 = 5
  Placement = pos=(0,0,0) rot=(1,0,0;1.5708rad)
  Profile = -> Sketch021
  ReferenceAxis = -> Sketch021 [N_Axis]
  Refine = true
  Suppressed = false
  Type = 0
FEATURE [PartDesign::Body] Body001  label="Motor_Mount"
  AllowCompound = false
  Group = -> [Sketch002,Pad001,Sketch003,Pocket001,Sketch004,Pocket002,Sketch005,Pocket003,Chamfer,Sketch006,Pocket004,Chamfer001,Sketch011,Pad005,Sketch012,Pad006,Sketch013,Pad007,Sketch014,Pad008,Hole,Sketch015,Sketch016,Pocket006,Sketch017,Pad010,Sketch018,Pad011,Sketch019,Pad012,Sketch020,Pocket007,Sketch021,Pocket008]
  Origin = -> Origin001
  Placement = pos=(-26,-25,130) rot=(-0.57735,0.57735,0.57735;2.0944rad)
  Tip = -> Pocket008
COMPONENT P1 — recipe-attached ("Single_Block001", modeled in this document).
Construction recipe (the document's own serialized feature program — sketch geometry with constraints, then the solid features built on it; lengths are millimeters unless a unit is written):

FEATURE [Sketcher::SketchObject] Sketch
  ArcFitTolerance = 1e-06
  AttachmentSupport = -> [XZ_Plane]
  FullyConstrained = true
  MakeInternals = false
  MapMode = 5
  Placement = pos=(0,0,0) rot=(1,0,0;1.5708rad)
  sketch-geometry (6):
    g0: LineSegment StartX=0 StartY=0 StartZ=0 EndX=19.3 EndY=0 EndZ=0
    g1: LineSegment StartX=19.3 StartY=0 StartZ=0 EndX=16.3 EndY=13 EndZ=0
    g2: LineSegment StartX=16.3 StartY=13 StartZ=0 EndX=3 EndY=13 EndZ=0
    g3: LineSegment StartX=3 StartY=13 StartZ=0 EndX=0 EndY=0 EndZ=0
    g4: LineSegment [constr] StartX=16.3 StartY=13 StartZ=0 EndX=19.3 EndY=13 EndZ=0
    g5: LineSegment [constr] StartX=19.3 StartY=13 StartZ=0 EndX=19.3 EndY=0 EndZ=0
  constraints (16):
    c: Coincident(g-1,g0)
    c: PointOnObject(g0,g-1)
    c: Coincident(g0,g1)
    c: Coincident(g1,g2)
    c: Horizontal(g2)
    c: Coincident(g2,g3)
    c: Coincident(g3,g0)
    c: Equal(g3,g1)
    c: DistanceX(g2,g2) = 13.3
    c: Coincident(g1,g4)
    c: Horizontal(g4)
    c: Coincident(g4,g5)
    c: Coincident(g5,g0)
    c: Vertical(g5)
    c: DistanceY(g5,g5) = 13
    c: DistanceX(g4,g4) = 3
FEATURE [PartDesign::Pad] Pad
  Direction = (0,-1,2e-16)
  Length = 55
  Length2 = 10
  Placement = pos=(0,0,0) rot=(1,0,0;1.5708rad)
  Profile = -> Sketch
  ReferenceAxis = -> Sketch [N_Axis]
  Refine = true
  Suppressed = false
  Type = 0
FEATURE [Sketcher::SketchObject] Sketch001
  ArcFitTolerance = 1e-06
  AttachmentSupport = -> [Pad]
  ExternalGeometry = -> [Pad]
  FullyConstrained = true
  MakeInternals = false
  MapMode = 5
  Placement = pos=(0,5.7e-15,13) rot=(0,0,1;3.14159rad)
  sketch-geometry (5):
    g0: Circle CenterX=-9.65 CenterY=6.5 CenterZ=0 NormalX=0 NormalY=0 NormalZ=1 AngleXU=0 Radius=2.3
    g1: Circle CenterX=-9.65 CenterY=48.5 CenterZ=0 NormalX=0 NormalY=0 NormalZ=1 AngleXU=0 Radius=2.3
    g2: LineSegment [constr] StartX=-9.65 StartY=6.5 StartZ=0 EndX=-9.65 EndY=48.5 EndZ=0
    g3: LineSegment [constr] StartX=-9.65 StartY=48.5 StartZ=0 EndX=-9.65 EndY=55 EndZ=0
    g4: LineSegment [constr] StartX=-9.65 StartY=6.5 StartZ=0 EndX=-9.65 EndY=0 EndZ=0
  constraints (12):
    c: Coincident(g2,g0)
    c: Coincident(g2,g1)
    c: Vertical(g2)
    c: Coincident(g3,g1)
    c: Symmetric(g-6,g-6,g3)
    c: Vertical(g3)
    c: Coincident(g4,g0)
    c: Symmetric(g-5,g-5,g4)
    c: Equal(g0,g1)
    c: DistanceY(g2,g2) = 42
    c: Equal(g3,g4)
    c: Diameter(g1) = 4.6
FEATURE [PartDesign::Pocket] Pocket
  BaseFeature = -> Pad
  Direction = (0,0,-1)
  Length = 5
  Length2 = 5
  Placement = pos=(0,0,0) rot=(1,0,0;1.5708rad)
  Profile = -> Sketch001
  ReferenceAxis = -> Sketch001 [N_Axis]
  Refine = true
  Suppressed = false
  Type = 1
FEATURE [Sketcher::SketchObject] Sketch022
  ArcFitTolerance = 1e-06
  AttachmentSupport = -> [Pocket]
  ExternalGeometry = -> [Pocket]
  FullyConstrained = true
  MakeInternals = false
  MapMode = 5
  Placement = pos=(0,-55,1.21e-14) rot=(1,0,0;1.5708rad)
  sketch-geometry (34):
    g0: LineSegment StartX=16.3 StartY=13 StartZ=0 EndX=19.3 EndY=0 EndZ=0
    g1: LineSegment StartX=19.3 StartY=0 StartZ=0 EndX=0 EndY=0 EndZ=0
    g2: LineSegment StartX=0 StartY=0 StartZ=0 EndX=-3 EndY=13 EndZ=0
    g3: LineSegment StartX=-3 StartY=13 StartZ=0 EndX=-3 EndY=47.3 EndZ=0
    g4: LineSegment StartX=-3 StartY=47.3 StartZ=0 EndX=16.3 EndY=47.3 EndZ=0
    g5: LineSegment StartX=16.3 StartY=13 StartZ=0 EndX=16.3 EndY=18.3 EndZ=0
    g6: LineSegment StartX=16.3 StartY=18.3 StartZ=0 EndX=16.3 EndY=24.3 EndZ=0
    g7: LineSegment StartX=16.3 StartY=47.3 StartZ=0 EndX=16.3 EndY=44.3 EndZ=0
    g8: LineSegment StartX=16.3 StartY=44.3 StartZ=0 EndX=16.3 EndY=24.3 EndZ=0
    g9: ArcOfCircle [constr] CenterX=2.05 CenterY=41.75 CenterZ=0 NormalX=0 NormalY=0 NormalZ=1 AngleXU=0 Radius=1.5 StartAngle=1.5708 EndAngle=4.71239
    g10: ArcOfCircle [constr] CenterX=11.25 CenterY=41.75 CenterZ=0 NormalX=0 NormalY=0 NormalZ=1 AngleXU=0 Radius=1.5 StartAngle=4.71239 EndAngle=7.85398
    g11: LineSegment [constr] StartX=2.05 StartY=43.25 StartZ=0 EndX=11.25 EndY=43.25 EndZ=0
    g12: LineSegment [constr] StartX=2.05 StartY=40.25 StartZ=0 EndX=11.25 EndY=40.25 EndZ=0
    g13: ArcOfCircle [constr] CenterX=2.05 CenterY=26.85 CenterZ=0 NormalX=0 NormalY=0 NormalZ=1 AngleXU=0 Radius=1.5 StartAngle=1.5708 EndAngle=4.71239
    g14: ArcOfCircle [constr] CenterX=11.25 CenterY=26.85 CenterZ=0 NormalX=0 NormalY=0 NormalZ=1 AngleXU=0 Radius=1.5 StartAngle=4.71239 EndAngle=7.85398
    g15: LineSegment [constr] StartX=2.05 StartY=28.35 StartZ=0 EndX=11.25 EndY=28.35 EndZ=0
    g16: LineSegment [constr] StartX=2.05 StartY=25.35 StartZ=0 EndX=11.25 EndY=25.35 EndZ=0
    g17: LineSegment [constr] StartX=2.05 StartY=41.75 StartZ=0 EndX=2.05 EndY=26.85 EndZ=0
    g18: LineSegment [constr] StartX=11.25 StartY=41.75 StartZ=0 EndX=11.25 EndY=26.85 EndZ=0
    g19: LineSegment [constr] StartX=16.3 StartY=24.3 StartZ=0 EndX=-3 EndY=24.3 EndZ=0
    g20: LineSegment [constr] StartX=16.3 StartY=44.3 StartZ=0 EndX=-3 EndY=44.3 EndZ=0
    g21: LineSegment [constr] StartX=6.65 StartY=24.3 StartZ=0 EndX=6.65 EndY=25.35 EndZ=0
    g22: LineSegment [constr] StartX=6.65 StartY=43.25 StartZ=0 EndX=6.65 EndY=44.3 EndZ=0
    g23: ArcOfCircle CenterX=2.05 CenterY=41.75 CenterZ=0 NormalX=0 NormalY=0 NormalZ=1 AngleXU=0 Radius=2.25 StartAngle=1.5708 EndAngle=4.71239
    g24: ArcOfCircle CenterX=11.25 CenterY=41.75 CenterZ=0 NormalX=0 NormalY=0 NormalZ=1 AngleXU=0 Radius=2.25 StartAngle=4.71239 EndAngle=7.85398
    g25: LineSegment StartX=2.05 StartY=44 StartZ=0 EndX=11.25 EndY=44 EndZ=0
    g26: LineSegment StartX=2.05 StartY=39.5 StartZ=0 EndX=11.25 EndY=39.5 EndZ=0
    g27: ArcOfCircle CenterX=2.05 CenterY=26.85 CenterZ=0 NormalX=0 NormalY=0 NormalZ=1 AngleXU=0 Radius=2.25 StartAngle=1.5708 EndAngle=4.71239
    g28: ArcOfCircle CenterX=11.25 CenterY=26.85 CenterZ=0 NormalX=0 NormalY=0 NormalZ=1 AngleXU=0 Radius=2.25 StartAngle=4.71239 EndAngle=7.85398
    g29: LineSegment StartX=2.05 StartY=29.1 StartZ=0 EndX=11.25 EndY=29.1 EndZ=0
    g30: LineSegment StartX=2.05 StartY=24.6 StartZ=0 EndX=11.25 EndY=24.6 EndZ=0
    g31: LineSegment [constr] StartX=-0.2 StartY=41.75 StartZ=0 EndX=-3 EndY=41.75 EndZ=0
    g32: LineSegment [constr] StartX=-3 StartY=13 StartZ=0 EndX=0 EndY=13 EndZ=0
    g33: LineSegment [constr] StartX=0 StartY=13 StartZ=0 EndX=3 EndY=13 EndZ=0
  constraints (84):
    c: Coincident(g0,g-6)
    c: Coincident(g1,g-6)
    c: Coincident(g1,g-5)
    c: Coincident(g2,g-5)
    c: Vertical(g3)
    c: Coincident(g4,g3)
    c: Horizontal(g4)
    c: Coincident(g0,g-4)
    c: Coincident(g5,g0)
    c: Vertical(g5)
    c: Coincident(g6,g5)
    c: Vertical(g6)
    c: Coincident(g7,g4)
    c: Vertical(g7)
    c: Coincident(g8,g7)
    c: Coincident(g8,g6)
    c: Vertical(g8)
    c: DistanceY(g5,g5) = 5.3
    c: DistanceY(g8,g8) = 20
    c: DistanceY(g7,g7) = 3
    c: DistanceY(g6,g6) = 6
    c: Tangent(g9,g11) = 1.5708
    c: Tangent(g9,g12) = -1.5708
    c: Tangent(g10,g11) = 1.5708
    c: Tangent(g10,g12) = -1.5708
    c: Equal(g9,g10)
    c: Radius(g9) = 1.5
    c: Horizontal(g11)
    c: Tangent(g13,g15) = 1.5708
    c: Tangent(g13,g16) = -1.5708
    c: Tangent(g14,g15) = 1.5708
    c: Tangent(g14,g16) = -1.5708
    c: Equal(g13,g14)
    c: Horizontal(g15)
    c: Equal(g14,g10)
    c: Coincident(g17,g9)
    c: Coincident(g17,g13)
    c: Vertical(g17)
    c: Coincident(g18,g10)
    c: Coincident(g18,g14)
    c: Vertical(g18)
    c: Coincident(g19,g6)
    c: PointOnObject(g19,g3)
    c: Horizontal(g19)
    c: Coincident(g20,g7)
    c: PointOnObject(g20,g3)
    c: Horizontal(g20)
    c: Symmetric(g19,g19,g21)
    c: Symmetric(g16,g16,g21)
    c: Vertical(g21)
    c: Symmetric(g11,g11,g22)
    c: Symmetric(g20,g20,g22)
    c: Equal(g22,g21)
    c: DistanceY(g22,g22) = 1.05
    c: Tangent(g23,g25) = 1.5708
    c: Tangent(g23,g26) = -1.5708
    c: Tangent(g24,g25) = 1.5708
    c: Tangent(g24,g26) = -1.5708
    c: Equal(g23,g24)
    c: Coincident(g23,g9)
    c: Coincident(g24,g10)
    c: Tangent(g27,g29) = 1.5708
    c: Tangent(g27,g30) = -1.5708
    c: Tangent(g28,g29) = 1.5708
    c: Tangent(g28,g30) = -1.5708
    c: Equal(g27,g28)
    c: Distance(g26,g12) = 0.75
    c: Equal(g24,g28)
    c: Coincident(g27,g13)
    c: Coincident(g28,g14)
    c: PointOnObject(g31,g23)
    c: PointOnObject(g31,g3)
    c: Horizontal(g31)
    c: Perpendicular(g23,g31)
    c: Distance(g31,g31) = 2.8
    c: Coincident(g2,g3)
    c: DistanceX(g16,g16) = 9.2
    c: Coincident(g2,g32)
    c: Horizontal(g32)
    c: Coincident(g32,g33)
    c: Coincident(g33,g-5)
    c: Horizontal(g33)
    c: Equal(g33,g32)
    c: PointOnObject(g32,g-2)
FEATURE [PartDesign::Pad] Pad013
  BaseFeature = -> Pocket
  Direction = (0,-1,2e-16)
  Length = 5
  Length2 = 10
  Placement = pos=(0,0,0) rot=(1,0,0;1.5708rad)
  Profile = -> Sketch022
  ReferenceAxis = -> Sketch022 [N_Axis]
  Refine = true
  Suppressed = false
  Type = 0
FEATURE [Sketcher::SketchObject] Sketch023
  ArcFitTolerance = 1e-06
  AttachmentSupport = -> [Pad013]
  ExternalGeometry = -> [Pad013]
  FullyConstrained = true
  MakeInternals = false
  MapMode = 5
  Placement = pos=(0,-55,0) rot=(-1,0,0;1.5708rad)
  sketch-geometry (14):
    g0: LineSegment StartX=10.25 StartY=-30.55 StartZ=0 EndX=10.25 EndY=-38.05 EndZ=0
    g1: LineSegment StartX=10.25 StartY=-38.05 StartZ=0 EndX=3.05 EndY=-38.05 EndZ=0
    g2: LineSegment StartX=3.05 StartY=-38.05 StartZ=0 EndX=3.05 EndY=-39.3 EndZ=0
    g3: LineSegment StartX=3.05 StartY=-39.3 StartZ=0 EndX=-3 EndY=-39.3 EndZ=0
    g4: LineSegment StartX=-3 StartY=-39.3 StartZ=0 EndX=-3 EndY=-31.05 EndZ=0
    g5: LineSegment StartX=-3 StartY=-31.05 StartZ=0 EndX=0.85 EndY=-31.05 EndZ=0
    g6: LineSegment StartX=0.85 StartY=-31.05 StartZ=0 EndX=0.85 EndY=-30.55 EndZ=0
    g7: LineSegment StartX=0.85 StartY=-30.55 StartZ=0 EndX=10.25 EndY=-30.55 EndZ=0
    g8: LineSegment StartX=4.25 StartY=-29.1 StartZ=0 EndX=-3 EndY=-29.1 EndZ=0
    g9: LineSegment StartX=-3 StartY=-29.1 StartZ=0 EndX=-3 EndY=-25.75 EndZ=0
    g10: LineSegment StartX=-3 StartY=-25.75 StartZ=0 EndX=4.25 EndY=-25.75 EndZ=0
    g11: LineSegment StartX=4.25 StartY=-25.75 StartZ=0 EndX=4.25 EndY=-29.1 EndZ=0
    g12: LineSegment [constr] StartX=13.5 StartY=-26.85 StartZ=0 EndX=13.5 EndY=-29.1 EndZ=0
    g13: LineSegment [constr] StartX=13.5 StartY=-29.1 StartZ=0 EndX=4.25 EndY=-29.1 EndZ=0
  constraints (41):
    c: Vertical(g0)
    c: Coincident(g0,g1)
    c: Horizontal(g1)
    c: Coincident(g1,g2)
    c: Vertical(g2)
    c: Coincident(g2,g3)
    c: Horizontal(g3)
    c: Coincident(g3,g4)
    c: Vertical(g4)
    c: Coincident(g4,g5)
    c: Horizontal(g5)
    c: Coincident(g5,g6)
    c: Vertical(g6)
    c: Coincident(g6,g7)
    c: Coincident(g7,g0)
    c: Horizontal(g7)
    c: Horizontal(g8)
    c: Coincident(g8,g9)
    c: Vertical(g9)
    c: Coincident(g9,g10)
    c: Horizontal(g10)
    c: Coincident(g10,g11)
    c: Coincident(g11,g8)
    c: Vertical(g11)
    c: Vertical(g12)
    c: Tangent(g12,g-8) = 1.5708
    c: Coincident(g13,g12)
    c: Coincident(g13,g8)
    c: Horizontal(g13)
    c: DistanceX(g13,g13) = 9.25
    c: PointOnObject(g8,g-10)
    c: DistanceY(g9,g9) = 3.35
    c: DistanceY(g0,g0) = 7.5
    c: DistanceY(g2,g2) = 1.25
    c: DistanceY(g12,g12) = 2.25
    c: Distance(g-12,g1) = 3.7
    c: DistanceX(g1,g1) = 7.2
    c: DistanceX(g0,g-12) = 1
    c: DistanceX(g6,g-9) = 1.2
    c: DistanceY(g4,g4) = 8.25
    c: PointOnObject(g3,g-10)
FEATURE [PartDesign::Pocket] Pocket009
  BaseFeature = -> Pad013
  Direction = (0,-1,-2e-16)
  Length = 2.5
  Length2 = 5
  Placement = pos=(0,0,0) rot=(1,0,0;1.5708rad)
  Profile = -> Sketch023
  ReferenceAxis = -> Sketch023 [N_Axis]
  Refine = true
  Suppressed = false
  Type = 0
FEATURE [PartDesign::Chamfer] Chamfer005
  Angle = 45
  Base = -> Pocket009 [Edge57,Edge45,Edge17,Edge56,Edge44,Edge46,Edge43,Edge40,Edge34]
  BaseFeature = -> Pocket009
  ChamferType = 0
  FlipDirection = false
  Placement = pos=(0,0,0) rot=(1,0,0;1.5708rad)
  Refine = true
  Size = 1
  Size2 = 1
  SupportTransform = false
  Suppressed = false
  UseAllEdges = false
FEATURE [PartDesign::Body] Body  label="Single_Block"
  AllowCompound = false
  Group = -> [Sketch,Pad,Sketch001,Pocket,Sketch022,Pad013,Sketch023,Pocket009,Chamfer005]
  Origin = -> Origin
  Placement = pos=(-26,-25,-23) rot=(-0.57735,0.57735,0.57735;2.0944rad)
  Tip = -> Chamfer005
COMPONENT P2 — recipe-attached ("Window_Grab_Arm001", modeled in this document).
Construction recipe (the document's own serialized feature program — sketch geometry with constraints, then the solid features built on it; lengths are millimeters unless a unit is written):

FEATURE [Sketcher::SketchObject] Sketch007
  ArcFitTolerance = 1e-06
  AttachmentSupport = -> [XY_Plane002]
  FullyConstrained = true
  MakeInternals = false
  MapMode = 5
  expr: Constraints[122] = 3.9 + 0.35
  expr: Constraints[72] = (2.9 + 0.2) / 2
  expr: Constraints[73] = (10 + 0.5) / 2
  sketch-geometry (53):
    g0: ArcOfCircle CenterX=0 CenterY=0 CenterZ=0 NormalX=0 NormalY=0 NormalZ=1 AngleXU=0 Radius=14.35 StartAngle=4.71239 EndAngle=7.85398
    g1: ArcOfCircle CenterX=-20 CenterY=9e-16 CenterZ=0 NormalX=0 NormalY=0 NormalZ=1 AngleXU=0 Radius=14.35 StartAngle=3.92699 EndAngle=4.71239
    g2: ArcOfCircle CenterX=-41.666 CenterY=21.666 CenterZ=0 NormalX=0 NormalY=0 NormalZ=1 AngleXU=0 Radius=14.35 StartAngle=3.14159 EndAngle=3.92699
    g3: ArcOfCircle CenterX=0 CenterY=7.8 CenterZ=0 NormalX=0 NormalY=0 NormalZ=1 AngleXU=0 Radius=1.55 StartAngle=4.71239 EndAngle=7.85398
    g4: ArcOfCircle CenterX=-20 CenterY=7.8 CenterZ=0 NormalX=0 NormalY=0 NormalZ=1 AngleXU=0 Radius=1.55 StartAngle=1.5708 EndAngle=4.71239
    g5: ArcOfCircle CenterX=-20 CenterY=-7.8 CenterZ=0 NormalX=0 NormalY=0 NormalZ=1 AngleXU=0 Radius=1.55 StartAngle=1.5708 EndAngle=4.71239
    g6: ArcOfCircle CenterX=0 CenterY=-7.8 CenterZ=0 NormalX=0 NormalY=0 NormalZ=1 AngleXU=0 Radius=1.55 StartAngle=4.71239 EndAngle=7.85398
    g7: ArcOfCircle CenterX=7.8 CenterY=-3e-16 CenterZ=0 NormalX=0 NormalY=0 NormalZ=1 AngleXU=0 Radius=1.55 StartAngle=4.71239 EndAngle=7.85398
    g8: ArcOfCircle CenterX=-27.8 CenterY=1.7e-15 CenterZ=0 NormalX=0 NormalY=0 NormalZ=1 AngleXU=0 Radius=1.55 StartAngle=1.5708 EndAngle=4.71239
    g9: LineSegment StartX=-20 StartY=9.35 StartZ=0 EndX=0 EndY=9.35 EndZ=0
    g10: LineSegment StartX=-20 StartY=6.25 StartZ=0 EndX=0 EndY=6.25 EndZ=0
    g11: LineSegment StartX=-20 StartY=5.25 StartZ=0 EndX=0 EndY=5.25 EndZ=0
    g12: LineSegment StartX=-20 StartY=-5.25 StartZ=0 EndX=0 EndY=-5.25 EndZ=0
    g13: LineSegment StartX=-20 StartY=-6.25 StartZ=0 EndX=0 EndY=-6.25 EndZ=0
    g14: LineSegment StartX=-20 StartY=-9.35 StartZ=0 EndX=0 EndY=-9.35 EndZ=0
    g15: LineSegment StartX=-20 StartY=-14.35 StartZ=0 EndX=-3.6e-15 EndY=-14.35 EndZ=0
    g16: LineSegment StartX=-27.8 StartY=1.55 StartZ=0 EndX=-25.016 EndY=1.55 EndZ=0
    g17: LineSegment StartX=-27.8 StartY=-1.55 StartZ=0 EndX=-25.016 EndY=-1.55 EndZ=0
    g18: LineSegment StartX=5.01597 StartY=1.55 StartZ=0 EndX=7.8 EndY=1.55 EndZ=0
    g19: LineSegment StartX=7.8 StartY=-1.55 StartZ=0 EndX=5.01597 EndY=-1.55 EndZ=0
    g20: LineSegment StartX=4.4e-15 StartY=14.35 StartZ=0 EndX=-20 EndY=14.35 EndZ=0
    g21: LineSegment StartX=-51.813 StartY=11.519 StartZ=0 EndX=-30.147 EndY=-10.147 EndZ=0
    g22: LineSegment StartX=-56.016 StartY=21.666 StartZ=0 EndX=-56.016 EndY=59.35 EndZ=0
    g23: LineSegment [constr] StartX=-20 StartY=-1e-16 StartZ=0 EndX=-20 EndY=7.8 EndZ=0
    g24: LineSegment [constr] StartX=-20 StartY=-7.8 StartZ=0 EndX=-20 EndY=0 EndZ=0
    g25: LineSegment [constr] StartX=0 StartY=-7.8 StartZ=0 EndX=0 EndY=0 EndZ=0
    g26: LineSegment [constr] StartX=0 StartY=0 StartZ=0 EndX=0 EndY=7.8 EndZ=0
    g27: LineSegment [constr] StartX=0 StartY=0 StartZ=0 EndX=7.8 EndY=-3e-16 EndZ=0
    g28: LineSegment [constr] StartX=-27.8 StartY=1.7e-15 StartZ=0 EndX=-20 EndY=-1e-16 EndZ=0
    g29: ArcOfCircle CenterX=0 CenterY=0 CenterZ=0 NormalX=0 NormalY=0 NormalZ=1 AngleXU=0 Radius=5.25 StartAngle=0.299705 EndAngle=1.5708
    g30: ArcOfCircle CenterX=0 CenterY=0 CenterZ=0 NormalX=0 NormalY=0 NormalZ=1 AngleXU=0 Radius=5.25 StartAngle=4.71239 EndAngle=5.98348
    g31: ArcOfCircle CenterX=-20 CenterY=-1e-16 CenterZ=0 NormalX=0 NormalY=0 NormalZ=1 AngleXU=0 Radius=5.25 StartAngle=1.5708 EndAngle=2.84189
    g32: ArcOfCircle CenterX=-20 CenterY=-1e-16 CenterZ=0 NormalX=0 NormalY=0 NormalZ=1 AngleXU=0 Radius=5.25 StartAngle=3.4413 EndAngle=4.71239
    g33: LineSegment StartX=-21.4142 StartY=14.9358 StartZ=0 EndX=-26.7302 EndY=20.2518 EndZ=0
    g34: LineSegment StartX=-27.316 StartY=21.666 StartZ=0 EndX=-27.316 EndY=57.2287 EndZ=0
    g35: ArcOfCircle CenterX=-25.316 CenterY=21.666 CenterZ=0 NormalX=0 NormalY=0 NormalZ=1 AngleXU=0 Radius=2 StartAngle=3.14159 EndAngle=3.92699
    g36: ArcOfCircle CenterX=-20 CenterY=16.35 CenterZ=0 NormalX=0 NormalY=0 NormalZ=1 AngleXU=0 Radius=2 StartAngle=3.92699 EndAngle=4.71239
    g37: LineSegment StartX=-27.316 StartY=57.2287 StartZ=0 EndX=-29.4373 EndY=59.35 EndZ=0
    g38: LineSegment StartX=-56.016 StartY=59.35 StartZ=0 EndX=-29.4373 EndY=59.35 EndZ=0
    g39: LineSegment [constr] StartX=-20 StartY=-14.35 StartZ=0 EndX=-56.016 EndY=-14.35 EndZ=0
    g40: LineSegment [constr] StartX=-56.016 StartY=-14.35 StartZ=0 EndX=-56.016 EndY=21.666 EndZ=0
    g41: LineSegment [constr] StartX=-47.766 StartY=59.35 StartZ=0 EndX=-47.766 EndY=-14.35 EndZ=0
    g42: LineSegment [constr] StartX=-44.016 StartY=59.35 StartZ=0 EndX=-44.016 EndY=-14.35 EndZ=0
    g43: Circle CenterX=-35.691 CenterY=50.975 CenterZ=0 NormalX=0 NormalY=0 NormalZ=1 AngleXU=0 Radius=2.125
    g44: Circle CenterX=-35.691 CenterY=40.475 CenterZ=0 NormalX=0 NormalY=0 NormalZ=1 AngleXU=0 Radius=2.125
    g45: Circle CenterX=-35.691 CenterY=29.975 CenterZ=0 NormalX=0 NormalY=0 NormalZ=1 AngleXU=0 Radius=2.125
    g46: LineSegment [constr] StartX=-35.691 StartY=53.1 StartZ=0 EndX=-35.691 EndY=59.35 EndZ=0
    g47: LineSegment [constr] StartX=-35.691 StartY=48.85 StartZ=0 EndX=-35.691 EndY=42.6 EndZ=0
    g48: LineSegment [constr] StartX=-35.691 StartY=38.35 StartZ=0 EndX=-35.691 EndY=32.1 EndZ=0
    g49: LineSegment [constr] StartX=-56.016 StartY=21.666 StartZ=0 EndX=-27.316 EndY=21.666 EndZ=0
    g50: LineSegment [constr] StartX=-33.566 StartY=50.975 StartZ=0 EndX=-27.316 EndY=50.975 EndZ=0
    g51: LineSegment [constr] StartX=-20 StartY=7.8 StartZ=0 EndX=-20 EndY=14.35 EndZ=0
    g52: LineSegment [constr] StartX=-20 StartY=-7.8 StartZ=0 EndX=-20 EndY=-14.35 EndZ=0
  constraints (142):
    c: Horizontal(g9)
    c: Horizontal(g10)
    c: Horizontal(g11)
    c: Horizontal(g12)
    c: Horizontal(g13)
    c: Horizontal(g14)
    c: Horizontal(g15)
    c: Tangent(g9,g4) = 1.5708
    c: Tangent(g10,g4) = -1.5708
    c: Tangent(g10,g3) = -1.5708
    c: Tangent(g9,g3) = 1.5708
    c: Tangent(g13,g6) = 1.5708
    c: Tangent(g14,g6) = -1.5708
    c: Tangent(g13,g5) = 1.5708
    c: Tangent(g14,g5) = -1.5708
    c: Horizontal(g16)
    c: Horizontal(g18)
    c: Horizontal(g19)
    c: Horizontal(g17)
    c: Tangent(g16,g8) = 1.5708
    c: Tangent(g17,g8) = -1.5708
    c: Equal(g16,g17)
    c: Tangent(g18,g7) = 1.5708
    c: Tangent(g19,g7) = 1.5708
    c: Equal(g18,g19)
    c: Horizontal(g20)
    c: Tangent(g21,g1) = -1.5708
    c: Tangent(g21,g2) = -1.5708
    c: Angle(g15,g21) = 2.35619
    c: Vertical(g22)
    c: Tangent(g22,g2) = 1.5708
    c: Tangent(g15,g0) = -1.5708
    c: Tangent(g20,g0) = -1.5708
    c: Tangent(g15,g1) = -1.5708
    c: Coincident(g0,g-1)
    c: Coincident(g23,g4)
    c: Vertical(g23)
    c: Coincident(g24,g5)
    c: Coincident(g25,g6)
    c: Coincident(g25,g0)
    c: Coincident(g26,g0)
    c: Coincident(g26,g3)
    c: Vertical(g24)
    c: Vertical(g25)
    c: Vertical(g26)
    c: Equal(g23,g24)
    c: Coincident(g27,g0)
    c: Coincident(g27,g7)
    c: Coincident(g28,g8)
    c: Coincident(g29,g0)
    c: Coincident(g29,g18)
    c: Coincident(g30,g0)
    c: Coincident(g30,g19)
    c: Coincident(g31,g23)
    c: Coincident(g31,g16)
    c: Coincident(g32,g24)
    c: Coincident(g32,g17)
    c: Equal(g30,g29)
    c: Equal(g29,g32)
    c: Coincident(g24,g23)
    c: Coincident(g24,g28)
    c: Equal(g27,g26)
    c: Equal(g23,g28)
    c: Equal(g8,g4)
    c: Equal(g5,g4)
    c: Tangent(g31,g11) = 1.5708
    c: Tangent(g32,g12) = -1.5708
    c: Tangent(g29,g11) = 1.5708
    c: Tangent(g30,g12) = -1.5708
    c: Equal(g7,g8)
    c: DistanceX(g11,g11) = 20
    c: DistanceY(g26,g26) = 7.8
    c: Radius(g3) = 1.55
    c: Radius(g31) = 5.25
    c: Distance(g20,g9) = 5
    c: Vertical(g34)
    c: Equal(g35,g36)
    c: Equal(g2,g1)
    c: Equal(g1,g0)
    c: Radius(g36) = 2
    c: Tangent(g36,g20) = 1.5708
    c: Tangent(g36,g33) = 1.5708
    c: Tangent(g35,g33) = 1.5708
    c: Tangent(g35,g34) = 1.5708
    c: Parallel(g21,g33)
    c: Coincident(g37,g34)
    c: Coincident(g38,g22)
    c: Coincident(g38,g37)
    c: Horizontal(g38)
    c: Angle(g38,g37) = 2.35619
    c: Distance(g37,g37) = 3
    c: Tangent(g39,g1) = 1.5708
    c: Vertical(g40)
    c: Coincident(g2,g40)
    c: Coincident(g40,g39)
    c: PointOnObject(g41,g38)
    c: PointOnObject(g41,g39)
    c: Vertical(g41)
    c: PointOnObject(g42,g38)
    c: PointOnObject(g42,g39)
    c: Vertical(g42)
    c: Distance(g42,g22) = 12
    c: Distance(g42,g41) = 3.75
    c: Distance(g16,g42) = 19
    c: Distance(g20,g38) = 45
    c: Equal(g43,g44)
    c: Equal(g44,g45)
    c: PointOnObject(g46,g43)
    c: PointOnObject(g46,g38)
    c: Vertical(g46)
    c: PointOnObject(g47,g43)
    c: PointOnObject(g47,g44)
    c: Vertical(g47)
    c: PointOnObject(g48,g44)
    c: PointOnObject(g48,g45)
    c: Vertical(g48)
    c: Perpendicular(g43,g46)
    c: Perpendicular(g43,g47)
    c: Perpendicular(g44,g47)
    c: Perpendicular(g44,g48)
    c: Perpendicular(g45,g48)
    c: Equal(g47,g48)
    c: Diameter(g45) = 4.25
    c: Coincident(g49,g2)
    c: Coincident(g49,g34)
    c: Horizontal(g49)
    c: PointOnObject(g50,g43)
    c: PointOnObject(g50,g34)
    c: Horizontal(g50)
    c: Perpendicular(g43,g50)
    c: DistanceX(g50,g50) = 6.25
    c: Coincident(g51,g4)
    c: Coincident(g51,g20)
    c: Coincident(g52,g5)
    c: Coincident(g52,g1)
    c: Vertical(g52)
    c: Vertical(g51)
    c: Equal(g46,g47)
    c: Equal(g50,g46)
    c: Distance(g34,g22) = 28.7
    c: DistanceY(g22,g22) = 37.684
    c: Distance(g0,g38) = 59.35
FEATURE [PartDesign::Pad] Pad002
  Direction = (0,0,1)
  Length = 8
  Length2 = 10
  Profile = -> Sketch007
  ReferenceAxis = -> Sketch007 [N_Axis]
  Refine = true
  Suppressed = false
  Type = 0
FEATURE [Sketcher::SketchObject] Sketch008
  ArcFitTolerance = 1e-06
  AttachmentSupport = -> [Pad002]
  ExternalGeometry = -> [Pad002]
  FullyConstrained = true
  MakeInternals = false
  MapMode = 5
  Placement = pos=(0,59.35,0) rot=(0,0.707107,0.707107;3.14159rad)
  expr: Constraints[12] = 3.75 / 2
  sketch-geometry (5):
    g0: LineSegment StartX=56.016 StartY=7 StartZ=0 EndX=47.766 EndY=7 EndZ=0
    g1: LineSegment StartX=44.016 StartY=8 StartZ=0 EndX=44.016 EndY=7 EndZ=0
    g2: ArcOfCircle CenterX=45.891 CenterY=7 CenterZ=0 NormalX=0 NormalY=0 NormalZ=1 AngleXU=0 Radius=1.875 StartAngle=3.14159 EndAngle=6.28319
    g3: LineSegment StartX=44.016 StartY=8 StartZ=0 EndX=56.016 EndY=8 EndZ=0
    g4: LineSegment StartX=56.016 StartY=8 StartZ=0 EndX=56.016 EndY=7 EndZ=0
  constraints (14):
    c: PointOnObject(g0,g-4)
    c: Horizontal(g0)
    c: PointOnObject(g1,g-3)
    c: Vertical(g1)
    c: Coincident(g2,g0)
    c: Tangent(g2,g1) = -1.5708
    c: Perpendicular(g2,g0)
    c: Coincident(g3,g1)
    c: Coincident(g3,g-4)
    c: Coincident(g4,g3)
    c: Coincident(g4,g0)
    c: DistanceX(g3,g3) = 12
    c: Radius(g2) = 1.875
    c: DistanceY(g4,g4) = 1
FEATURE [PartDesign::Pocket] Pocket005
  BaseFeature = -> Pad002
  Direction = (0,-1,2e-16)
  Length = 5
  Length2 = 5
  Profile = -> Sketch008
  ReferenceAxis = -> Sketch008 [N_Axis]
  Refine = true
  Suppressed = false
  Type = 1
FEATURE [PartDesign::Chamfer] Chamfer003
  Angle = 45
  Base = -> Pocket005 [Edge15,Edge16,Edge1,Edge5,Edge6,Edge7,Edge8,Edge9,Edge10,Edge11,Edge12,Edge13,Edge14]
  BaseFeature = -> Pocket005
  ChamferType = 0
  FlipDirection = false
  Refine = true
  Size = 1
  Size2 = 1
  SupportTransform = false
  Suppressed = false
  UseAllEdges = false
FEATURE [PartDesign::Body] Body002  label="Window_Grab_Arm"
  AllowCompound = false
  Group = -> [Sketch007,Pad002,Sketch008,Pocket005,Chamfer003]
  Origin = -> Origin002
  Placement = pos=(11,3.5,0) rot=(0,0,1;0rad)
  Tip = -> Chamfer003
COMPONENT P3 — recipe-attached ("Window_Grab_Arm_Clamp001", modeled in this document).
Construction recipe (the document's own serialized feature program — sketch geometry with constraints, then the solid features built on it; lengths are millimeters unless a unit is written):

FEATURE [Sketcher::SketchObject] Sketch010
  ArcFitTolerance = 1e-06
  AttachmentSupport = -> [XY_Plane004]
  FullyConstrained = true
  MakeInternals = false
  MapMode = 5
  expr: Constraints[20] = 10 + 0.5
  sketch-geometry (11):
    g0: Circle CenterX=0 CenterY=0 CenterZ=0 NormalX=0 NormalY=0 NormalZ=1 AngleXU=0 Radius=14.35
    g1: Circle CenterX=0 CenterY=0 CenterZ=0 NormalX=0 NormalY=0 NormalZ=1 AngleXU=0 Radius=5.25
    g2: Circle CenterX=0 CenterY=7.8 CenterZ=0 NormalX=0 NormalY=0 NormalZ=1 AngleXU=0 Radius=1.5
    g3: Circle CenterX=7.8 CenterY=0 CenterZ=0 NormalX=0 NormalY=0 NormalZ=1 AngleXU=0 Radius=1.5
    g4: Circle CenterX=-7.8 CenterY=0 CenterZ=0 NormalX=0 NormalY=0 NormalZ=1 AngleXU=0 Radius=1.5
    g5: Circle CenterX=0 CenterY=-7.8 CenterZ=0 NormalX=0 NormalY=0 NormalZ=1 AngleXU=0 Radius=1.5
    g6: LineSegment [constr] StartX=0 StartY=0 StartZ=0 EndX=0 EndY=7.8 EndZ=0
    g7: LineSegment [constr] StartX=0 StartY=0 StartZ=0 EndX=-7.8 EndY=0 EndZ=0
    g8: LineSegment [constr] StartX=0 StartY=0 StartZ=0 EndX=0 EndY=-7.8 EndZ=0
    g9: LineSegment [constr] StartX=0 StartY=0 StartZ=0 EndX=7.8 EndY=0 EndZ=0
    g10: LineSegment [constr] StartX=0 StartY=7.8 StartZ=0 EndX=0 EndY=14.35 EndZ=0
  constraints (27):
    c: Coincident(g0,g-1)
    c: Coincident(g1,g0)
    c: PointOnObject(g2,g-2)
    c: PointOnObject(g3,g-1)
    c: PointOnObject(g4,g-1)
    c: PointOnObject(g5,g-2)
    c: Coincident(g6,g0)
    c: Coincident(g6,g2)
    c: Coincident(g7,g0)
    c: Coincident(g7,g4)
    c: Coincident(g8,g0)
    c: Coincident(g8,g5)
    c: Coincident(g9,g0)
    c: Coincident(g9,g3)
    c: Equal(g6,g7)
    c: Equal(g7,g9)
    c: Equal(g9,g8)
    c: Equal(g2,g4)
    c: Equal(g4,g5)
    c: Equal(g5,g3)
    c: Diameter(g1) = 10.5
    c: Diameter(g3) = 3
    c: DistanceY(g6,g6) = 7.8
    c: Coincident(g10,g2)
    c: PointOnObject(g10,g0)
    c: Vertical(g10)
    c: DistanceY(g10,g10) = 6.55
FEATURE [PartDesign::Pad] Pad004
  Direction = (0,0,1)
  Length = 5
  Length2 = 10
  Profile = -> Sketch010
  ReferenceAxis = -> Sketch010 [N_Axis]
  Refine = true
  Suppressed = false
  Type = 0
FEATURE [PartDesign::Chamfer] Chamfer002
  Angle = 45
  Base = -> Pad004 [Edge3]
  BaseFeature = -> Pad004
  ChamferType = 0
  FlipDirection = false
  Refine = true
  Size = 1
  Size2 = 1
  SupportTransform = false
  Suppressed = false
  UseAllEdges = false
FEATURE [PartDesign::Body] Body004  label="Window_Grab_Arm_Clamp"
  AllowCompound = false
  Group = -> [Sketch010,Pad004,Chamfer002]
  Origin = -> Origin004
  Placement = pos=(1.5,3.5,9) rot=(0,0,1;0rad)
  Tip = -> Chamfer002
COMPONENT P4 — recipe-attached ("Window_Grab_Clamp001", modeled in this document).
Construction recipe (the document's own serialized feature program — sketch geometry with constraints, then the solid features built on it; lengths are millimeters unless a unit is written):

FEATURE [Sketcher::SketchObject] Sketch009
  ArcFitTolerance = 1e-06
  AttachmentSupport = -> [XY_Plane003]
  FullyConstrained = true
  MakeInternals = false
  MapMode = 5
  expr: Constraints[16] = 3.9 + 0.35
  sketch-geometry (12):
    g0: LineSegment StartX=0 StartY=-2.12132 StartZ=0 EndX=-2.12132 EndY=0 EndZ=0
    g1: LineSegment StartX=-2.12132 StartY=0 StartZ=0 EndX=-28.7 EndY=0 EndZ=0
    g2: LineSegment StartX=-28.7 StartY=0 StartZ=0 EndX=-28.7 EndY=-37.684 EndZ=0
    g3: LineSegment StartX=-28.7 StartY=-37.684 StartZ=0 EndX=0 EndY=-37.684 EndZ=0
    g4: LineSegment StartX=0 StartY=-37.684 StartZ=0 EndX=0 EndY=-2.12132 EndZ=0
    g5: Circle CenterX=-8.375 CenterY=-8.375 CenterZ=0 NormalX=0 NormalY=0 NormalZ=1 AngleXU=0 Radius=2.125
    g6: Circle CenterX=-8.375 CenterY=-18.875 CenterZ=0 NormalX=0 NormalY=0 NormalZ=1 AngleXU=0 Radius=2.125
    g7: Circle CenterX=-8.375 CenterY=-29.375 CenterZ=0 NormalX=0 NormalY=0 NormalZ=1 AngleXU=0 Radius=2.125
    g8: LineSegment [constr] StartX=-8.375 StartY=0 StartZ=0 EndX=-8.375 EndY=-6.25 EndZ=0
    g9: LineSegment [constr] StartX=-6.25 StartY=-8.375 StartZ=0 EndX=0 EndY=-8.375 EndZ=0
    g10: LineSegment [constr] StartX=-8.375 StartY=-16.75 StartZ=0 EndX=-8.375 EndY=-10.5 EndZ=0
    g11: LineSegment [constr] StartX=-8.375 StartY=-27.25 StartZ=0 EndX=-8.375 EndY=-21 EndZ=0
  constraints (40):
    c: PointOnObject(g0,g-2)
    c: PointOnObject(g0,g-1)
    c: Coincident(g0,g1)
    c: PointOnObject(g1,g-1)
    c: Coincident(g1,g2)
    c: Vertical(g2)
    c: Coincident(g2,g3)
    c: PointOnObject(g3,g-2)
    c: Horizontal(g3)
    c: Coincident(g3,g4)
    c: Coincident(g4,g0)
    c: Distance(g0,g0) = 3
    c: Angle(g1,g0) = 2.35619
    c: DistanceY(g2,g2) = 37.684
    c: Equal(g6,g5)
    c: Equal(g5,g7)
    c: Diameter(g7) = 4.25
    c: PointOnObject(g8,g1)
    c: PointOnObject(g8,g5)
    c: Vertical(g8)
    c: PointOnObject(g9,g5)
    c: PointOnObject(g9,g4)
    c: PointOnObject(g10,g6)
    c: PointOnObject(g10,g5)
    c: Vertical(g10)
    c: PointOnObject(g11,g7)
    c: PointOnObject(g11,g6)
    c: Vertical(g11)
    c: Horizontal(g9)
    c: Perpendicular(g5,g8)
    c: Perpendicular(g5,g9)
    c: Perpendicular(g5,g10)
    c: Perpendicular(g6,g10)
    c: Perpendicular(g6,g11)
    c: Perpendicular(g7,g11)
    c: Equal(g9,g8)
    c: Equal(g8,g10)
    c: Equal(g10,g11)
    c: DistanceX(g9,g9) = 6.25
    c: Distance(g4,g2) = 28.7
FEATURE [PartDesign::Pad] Pad003
  Direction = (0,0,1)
  Length = 5
  Length2 = 10
  Profile = -> Sketch009
  ReferenceAxis = -> Sketch009 [N_Axis]
  Refine = true
  Suppressed = false
  Type = 0
FEATURE [PartDesign::Chamfer] Chamfer004
  Angle = 45
  Base = -> Pad003 [Edge10,Edge7,Edge4,Edge15,Edge13]
  BaseFeature = -> Pad003
  ChamferType = 0
  FlipDirection = false
  Refine = true
  Size = 1
  Size2 = 1
  SupportTransform = false
  Suppressed = false
  UseAllEdges = false
FEATURE [PartDesign::Body] Body003  label="Window_Grab_Clamp"
  AllowCompound = false
  Group = -> [Sketch009,Pad003,Chamfer004]
  Origin = -> Origin003
  Placement = pos=(-16.32,62.85,9) rot=(0,0,1;0rad)
  Tip = -> Chamfer004
PROVENANCE & LICENSES
A FreeCAD (.FCStd) document from a public repository crawl; recipes are the document's own serialized feature recipes (and, for linked parts, companion documents' recipes).
License: gpl-3.0.
